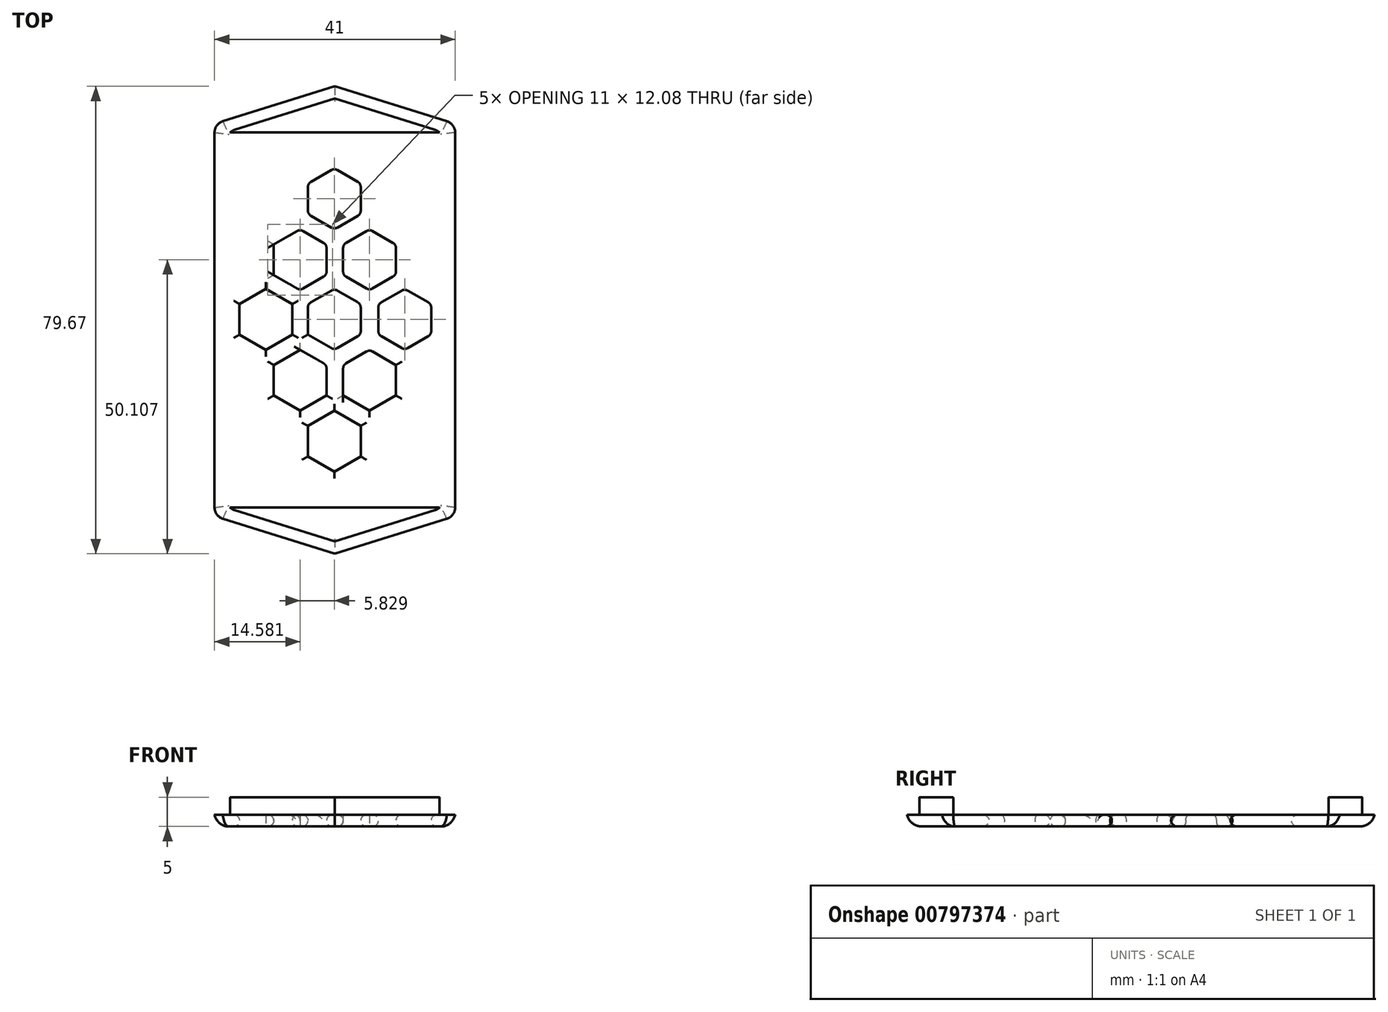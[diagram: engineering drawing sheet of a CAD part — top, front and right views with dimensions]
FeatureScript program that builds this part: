
annotation { "Feature Type Name" : "Feature", "Feature Type Description" : "" }
export const myFeature = defineFeature(function(context is Context, id is Id, definition is map)
    precondition{}
    {
        {
            var Q0;
            Q0=qCreatedBy(makeId("Top.planeOp"),FACE);
            var sketch = newSketch(context, id + "F0", { "sketchPlane" : qUnion([Q0])});
            skLineSegment(sketch, "E0", {"start": v(0.09, 44.17) * mm, "end": v(0.09, -36.2) * mm, "construction": true});
            skArc(sketch, "E1", {"start": v(-17, 32.29) * mm, "mid": v(-18.03, 31.56) * mm, "end": v(-18.41, 30.38) * mm});
            skLineSegment(sketch, "E2", {"start": v(-17, 32.29) * mm, "end": v(0.09, 37.62) * mm});
            skLineSegment(sketch, "E3", {"start": v(-66.44, -0.12) * mm, "end": v(70.75, -0.12) * mm, "construction": true});
            skLineSegment(sketch, "E4", {"start": v(-18.41, 30.38) * mm, "end": v(-18.41, -0.12) * mm});
            skLineSegment(sketch, "E5", {"start": v(-20.41, -0.12) * mm, "end": v(-20.41, 31.85) * mm});
            skLineSegment(sketch, "E6", {"start": v(0.09, 39.71) * mm, "end": v(-19, 33.76) * mm});
            skPoint(sketch, "E7.visualSharp", {"position": v(-20.41, 33.32) * mm});
            skArc(sketch, "E7.filletArc", {"start": v(-19, 33.76) * mm, "mid": v(-20.03, 33.03) * mm, "end": v(-20.41, 31.85) * mm});
            skArc(sketch, "E8.MirrorCS", {"start": v(19.18, 33.76) * mm, "mid": v(20.2, 33.03) * mm, "end": v(20.59, 31.85) * mm});
            skArc(sketch, "E9.MirrorC", {"start": v(17.18, 32.29) * mm, "mid": v(18.2, 31.56) * mm, "end": v(18.59, 30.38) * mm});
            skPoint(sketch, "E10.MirrorP", {"position": v(20.59, 33.32) * mm});
            skLineSegment(sketch, "E11.MirrorCS", {"start": v(18.59, 30.38) * mm, "end": v(18.59, -0.12) * mm});
            skLineSegment(sketch, "E12.MirrorCS", {"start": v(0.09, 39.71) * mm, "end": v(19.18, 33.76) * mm});
            skLineSegment(sketch, "E13.MirrorCS", {"start": v(17.18, 32.29) * mm, "end": v(0.09, 37.62) * mm});
            skLineSegment(sketch, "E14.MirrorCS", {"start": v(20.59, -0.12) * mm, "end": v(20.59, 31.85) * mm});
            skLineSegment(sketch, "E15.MirrorCS", {"start": v(66.62, -0.12) * mm, "end": v(-70.58, -0.12) * mm, "construction": true});
            skArc(sketch, "E16.MirrorCS", {"start": v(-19, -34) * mm, "mid": v(-20.03, -33.28) * mm, "end": v(-20.41, -32.1) * mm});
            skArc(sketch, "E17.MirrorCS", {"start": v(19.18, -34) * mm, "mid": v(20.2, -33.28) * mm, "end": v(20.59, -32.1) * mm});
            skArc(sketch, "E18.MirrorC", {"start": v(-17, -32.53) * mm, "mid": v(-18.03, -31.8) * mm, "end": v(-18.41, -30.62) * mm});
            skLineSegment(sketch, "E19.MirrorCS", {"start": v(-20.41, -0.12) * mm, "end": v(-20.41, -32.1) * mm});
            skPoint(sketch, "E20.MirrorP", {"position": v(20.59, -33.57) * mm});
            skLineSegment(sketch, "E21.MirrorCS", {"start": v(-17, -32.53) * mm, "end": v(0.09, -37.86) * mm});
            skArc(sketch, "E22.MirrorC", {"start": v(17.18, -32.53) * mm, "mid": v(18.2, -31.8) * mm, "end": v(18.59, -30.62) * mm});
            skLineSegment(sketch, "E23.MirrorCS", {"start": v(17.18, -32.53) * mm, "end": v(0.09, -37.86) * mm});
            skPoint(sketch, "E24.MirrorP", {"position": v(-20.41, -33.57) * mm});
            skLineSegment(sketch, "E25.MirrorCS", {"start": v(18.59, -30.62) * mm, "end": v(18.59, -0.12) * mm});
            skLineSegment(sketch, "E26.MirrorCS", {"start": v(20.59, -0.12) * mm, "end": v(20.59, -32.1) * mm});
            skLineSegment(sketch, "E27.MirrorCS", {"start": v(0.09, -39.96) * mm, "end": v(19.18, -34) * mm});
            skLineSegment(sketch, "E28.MirrorCS", {"start": v(-18.41, -30.62) * mm, "end": v(-18.41, -0.12) * mm});
            skLineSegment(sketch, "E29.MirrorCS", {"start": v(0.09, -39.96) * mm, "end": v(-19, -34) * mm});
            skPoint(sketch, "E30.start.orphan", {"position": v(-16.41, 28.38) * mm});
            skPoint(sketch, "E31.MirrorCS.start.orphan", {"position": v(16.59, 28.38) * mm});
            skPoint(sketch, "E32.MirrorCS.start.orphan", {"position": v(16.59, -28.62) * mm});
            skPoint(sketch, "E33.MirrorCS.start.orphan", {"position": v(-16.41, -28.62) * mm});
            skLineSegment(sketch, "E34", {"start": v(-18.41, -32.1) * mm, "end": v(18.59, -32.1) * mm});
            skLineSegment(sketch, "E35.MirrorCS", {"start": v(-18.41, 31.85) * mm, "end": v(18.59, 31.85) * mm});
            skSolve(sketch);
        }
        {
            var Q0;
            {var subQ4=sQuery(id+"F0.wireOp",EDGE,"E2");Q0=makeQuery(id+"F0.imprint","IMPRINT",FACE,{"disambiguationData":[TD([[makeQuery(id+"F0.imprint","IMPRINT",EDGE,{"derivedFrom":subQ4}),-1.0]])]});}
            var Q1;
            {var subQ4=sQuery(id+"F0.wireOp",EDGE,"E21.MirrorCS");Q1=makeQuery(id+"F0.imprint","IMPRINT",FACE,{"disambiguationData":[TD([[makeQuery(id+"F0.imprint","IMPRINT",EDGE,{"derivedFrom":subQ4}),1.0]])]});}
            extrude(context, id + "F1", {"entities" : qUnion([Q0, Q1]), "depth" : 3 * mm, "offsetDistance" : 25 * mm});
        }
        {
            var Q0;
            {var subQ12=sQuery(id+"F0.wireOp",EDGE,"E2");Q0=makeQuery(id+"F0.imprint","IMPRINT",FACE,{"disambiguationData":[TD([[makeQuery(id+"F0.imprint","IMPRINT",EDGE,{"derivedFrom":subQ12}),1.0]])]});}
            var Q1;
            {var subQ4=sQuery(id+"F0.wireOp",EDGE,"E2");Q1=makeQuery(id+"F0.imprint","IMPRINT",FACE,{"disambiguationData":[TD([[makeQuery(id+"F0.imprint","IMPRINT",EDGE,{"derivedFrom":subQ4}),-1.0]])]});}
            var Q2;
            {var subQ4=sQuery(id+"F0.wireOp",EDGE,"E21.MirrorCS");Q2=makeQuery(id+"F0.imprint","IMPRINT",FACE,{"disambiguationData":[TD([[makeQuery(id+"F0.imprint","IMPRINT",EDGE,{"derivedFrom":subQ4}),1.0]])]});}
            var Q3;
            {var subQ8=sQuery(id+"F0.wireOp",EDGE,"E4");Q3=makeQuery(id+"F0.imprint","IMPRINT",FACE,{"disambiguationData":[TD([[makeQuery(id+"F0.imprint","IMPRINT",EDGE,{"derivedFrom":subQ8}),1.0]])]});}
            extrude(context, id + "F2", {"entities" : qUnion([Q0, Q1, Q2, Q3]), "oppositeDirection" : true, "depth" : 2 * mm, "offsetDistance" : 25 * mm});
        }
        {
            var Q0;
            Q0=makeQuery(id+"F2.opExtrude","CAP_EDGE",EDGE,{"disambiguationData":[OSD([sQuery(id+"F0.wireOp",EDGE,"E14.MirrorCS"),sQuery(id+"F0.wireOp",EDGE,"E26.MirrorCS")])],"isStart":false});
            var Q1;
            Q1=makeQuery(id+"F2.opExtrude","CAP_EDGE",EDGE,{"disambiguationData":[OSD([sQuery(id+"F0.wireOp",EDGE,"E29.MirrorCS")])],"isStart":false});
            fillet(context, id + "F3", {"entities" : qUnion([Q0, Q1]), "radius" : 2.5 * mm, "tangentPropagation" : true, "allowEdgeOverflow" : false});
        }
        {
            var Q0;
            Q0=makeQuery(id+"F2.opExtrude","CAP_FACE",FACE,{"disambiguationData":[OSD([sQuery(id+"F0.wireOp",EDGE,"E5"),sQuery(id+"F0.wireOp",EDGE,"E6"),sQuery(id+"F0.wireOp",EDGE,"E7.filletArc"),sQuery(id+"F0.wireOp",EDGE,"E8.MirrorCS"),sQuery(id+"F0.wireOp",EDGE,"E12.MirrorCS"),sQuery(id+"F0.wireOp",EDGE,"E14.MirrorCS"),sQuery(id+"F0.wireOp",EDGE,"E16.MirrorCS"),sQuery(id+"F0.wireOp",EDGE,"E17.MirrorCS"),sQuery(id+"F0.wireOp",EDGE,"E19.MirrorCS"),sQuery(id+"F0.wireOp",EDGE,"E26.MirrorCS"),sQuery(id+"F0.wireOp",EDGE,"E27.MirrorCS"),sQuery(id+"F0.wireOp",EDGE,"E29.MirrorCS")])],"isStart":false});
            var sketch = newSketch(context, id + "F4", { "sketchPlane" : qUnion([Q0])});
            skCircle(sketch, "E36.cCircle", {"center": v(0, 0) * mm, "radius": 4.5 * mm, "construction": true});
            skLineSegment(sketch, "E36.0", {"start": v(-4.5, -2.6) * mm, "end": v(-4.5, 2.6) * mm});
            skLineSegment(sketch, "E36.1", {"start": v(-4.5, 2.6) * mm, "end": v(0, 5.2) * mm});
            skLineSegment(sketch, "E36.2", {"start": v(0, 5.2) * mm, "end": v(4.5, 2.6) * mm});
            skLineSegment(sketch, "E36.3", {"start": v(4.5, 2.6) * mm, "end": v(4.5, -2.6) * mm});
            skLineSegment(sketch, "E36.4", {"start": v(4.5, -2.6) * mm, "end": v(0, -5.2) * mm});
            skLineSegment(sketch, "E36.5", {"start": v(0, -5.2) * mm, "end": v(-4.5, -2.6) * mm});
            skPoint(sketch, "E36.0.midPoint", {"position": v(-4.5, 0) * mm});
            skLineSegment(sketch, "E37", {"start": v(-4.77, 9.68) * mm, "end": v(12, 0) * mm, "construction": true});
            skLineSegment(sketch, "E38.MirrorCS", {"start": v(1.5, 7.8) * mm, "end": v(6, 5.2) * mm});
            skLineSegment(sketch, "E39.MirrorCS", {"start": v(1.5, 13) * mm, "end": v(1.5, 7.8) * mm});
            skLineSegment(sketch, "E40.MirrorCS", {"start": v(6, 15.59) * mm, "end": v(1.5, 13) * mm});
            skLineSegment(sketch, "E41.MirrorCS", {"start": v(10.5, 13) * mm, "end": v(6, 15.59) * mm});
            skLineSegment(sketch, "E42.MirrorCS", {"start": v(10.5, 7.8) * mm, "end": v(10.5, 13) * mm});
            skLineSegment(sketch, "E43.MirrorCS", {"start": v(6, 5.2) * mm, "end": v(10.5, 7.8) * mm});
            skLineSegment(sketch, "E44.MirrorCS", {"start": v(-1.33, 13) * mm, "end": v(-1.33, 7.8) * mm});
            skLineSegment(sketch, "E45.MirrorCS", {"start": v(-5.83, 15.59) * mm, "end": v(-1.33, 13) * mm});
            skLineSegment(sketch, "E46.MirrorCS", {"start": v(-10.33, 13) * mm, "end": v(-5.83, 15.59) * mm});
            skLineSegment(sketch, "E47.MirrorCS", {"start": v(-10.33, 7.8) * mm, "end": v(-10.33, 13) * mm});
            skLineSegment(sketch, "E48.MirrorCS", {"start": v(-5.83, 5.2) * mm, "end": v(-10.33, 7.8) * mm});
            skLineSegment(sketch, "E49.MirrorCS", {"start": v(-1.33, 7.8) * mm, "end": v(-5.83, 5.2) * mm});
            skLineSegment(sketch, "E50.MirrorCS", {"start": v(6, -4.95) * mm, "end": v(10.5, -7.55) * mm});
            skLineSegment(sketch, "E51.MirrorCS", {"start": v(1.5, -7.55) * mm, "end": v(6, -4.95) * mm});
            skLineSegment(sketch, "E52.MirrorCS", {"start": v(1.5, -12.74) * mm, "end": v(1.5, -7.55) * mm});
            skLineSegment(sketch, "E53.MirrorCS", {"start": v(6, -15.34) * mm, "end": v(1.5, -12.74) * mm});
            skLineSegment(sketch, "E54.MirrorCS", {"start": v(10.5, -12.74) * mm, "end": v(6, -15.34) * mm});
            skLineSegment(sketch, "E55.MirrorCS", {"start": v(10.5, -7.55) * mm, "end": v(10.5, -12.74) * mm});
            skLineSegment(sketch, "E56.MirrorCS", {"start": v(-5.83, -4.95) * mm, "end": v(-10.33, -7.55) * mm});
            skLineSegment(sketch, "E57.MirrorCS", {"start": v(-1.33, -7.55) * mm, "end": v(-5.83, -4.95) * mm});
            skLineSegment(sketch, "E58.MirrorCS", {"start": v(-1.33, -12.74) * mm, "end": v(-1.33, -7.55) * mm});
            skLineSegment(sketch, "E59.MirrorCS", {"start": v(-5.83, -15.34) * mm, "end": v(-1.33, -12.74) * mm});
            skLineSegment(sketch, "E60.MirrorCS", {"start": v(-10.33, -12.74) * mm, "end": v(-5.83, -15.34) * mm});
            skLineSegment(sketch, "E61.MirrorCS", {"start": v(-10.33, -7.55) * mm, "end": v(-10.33, -12.74) * mm});
            skLineSegment(sketch, "E62", {"start": v(0, -13.61) * mm, "end": v(12.63, -20.9) * mm, "construction": true});
            skLineSegment(sketch, "E63.MirrorCS", {"start": v(4.5, -17.94) * mm, "end": v(0, -15.34) * mm});
            skLineSegment(sketch, "E64.MirrorCS", {"start": v(4.5, -23.14) * mm, "end": v(4.5, -17.94) * mm});
            skLineSegment(sketch, "E65.MirrorCS", {"start": v(0, -25.74) * mm, "end": v(4.5, -23.14) * mm});
            skLineSegment(sketch, "E66.MirrorCS", {"start": v(-4.5, -23.14) * mm, "end": v(0, -25.74) * mm});
            skLineSegment(sketch, "E67.MirrorCS", {"start": v(-4.5, -17.94) * mm, "end": v(-4.5, -23.14) * mm});
            skLineSegment(sketch, "E68.MirrorCS", {"start": v(0, -15.34) * mm, "end": v(-4.5, -17.94) * mm});
            skLineSegment(sketch, "E69.MirrorCS", {"start": v(0, 13.86) * mm, "end": v(12.63, 21.15) * mm, "construction": true});
            skLineSegment(sketch, "E70.MirrorCS", {"start": v(4.5, 18.19) * mm, "end": v(0, 15.59) * mm});
            skLineSegment(sketch, "E71.MirrorCS", {"start": v(0, 15.59) * mm, "end": v(-4.5, 18.19) * mm});
            skLineSegment(sketch, "E72.MirrorCS", {"start": v(-4.5, 18.19) * mm, "end": v(-4.5, 23.38) * mm});
            skLineSegment(sketch, "E73.MirrorCS", {"start": v(-4.5, 23.38) * mm, "end": v(0, 25.98) * mm});
            skLineSegment(sketch, "E74.MirrorCS", {"start": v(0, 25.98) * mm, "end": v(4.5, 23.38) * mm});
            skLineSegment(sketch, "E75.MirrorCS", {"start": v(4.5, 23.38) * mm, "end": v(4.5, 18.19) * mm});
            skLineSegment(sketch, "E76", {"start": v(6, 5.2) * mm, "end": v(6, -4.95) * mm, "construction": true});
            skLineSegment(sketch, "E77", {"start": v(-5.83, 5.2) * mm, "end": v(-5.83, -4.95) * mm, "construction": true});
            skLineSegment(sketch, "E78.MirrorCS", {"start": v(7.5, 2.6) * mm, "end": v(7.5, -2.6) * mm});
            skLineSegment(sketch, "E79.MirrorCS", {"start": v(7.5, -2.6) * mm, "end": v(12, -5.2) * mm});
            skLineSegment(sketch, "E80.MirrorCS", {"start": v(-6, -15.59) * mm, "end": v(2.79, -10.52) * mm, "construction": true});
            skLineSegment(sketch, "E81.MirrorCS", {"start": v(12, 5.2) * mm, "end": v(7.5, 2.6) * mm});
            skLineSegment(sketch, "E82.MirrorCS", {"start": v(16.5, 2.6) * mm, "end": v(12, 5.2) * mm});
            skLineSegment(sketch, "E83.MirrorCS", {"start": v(16.5, -2.6) * mm, "end": v(16.5, 2.6) * mm});
            skLineSegment(sketch, "E84.MirrorCS", {"start": v(12, -5.2) * mm, "end": v(16.5, -2.6) * mm});
            skLineSegment(sketch, "E85.MirrorCS", {"start": v(-7.16, -2.6) * mm, "end": v(-7.16, 2.6) * mm});
            skLineSegment(sketch, "E86.MirrorCS", {"start": v(-7.16, 2.6) * mm, "end": v(-11.66, 5.2) * mm});
            skLineSegment(sketch, "E87.MirrorCS", {"start": v(-11.66, 5.2) * mm, "end": v(-16.16, 2.6) * mm});
            skLineSegment(sketch, "E88.MirrorCS", {"start": v(-16.16, 2.6) * mm, "end": v(-16.16, -2.6) * mm});
            skLineSegment(sketch, "E89.MirrorCS", {"start": v(-16.16, -2.6) * mm, "end": v(-11.66, -5.2) * mm});
            skLineSegment(sketch, "E90.MirrorCS", {"start": v(-11.66, -5.2) * mm, "end": v(-7.16, -2.6) * mm});
            skSolve(sketch);
        }
        {
            var Q0;
            Q0=makeQuery(id+"F4.imprint","IMPRINT",FACE,{"disambiguationData":[TD([[makeQuery(id+"F4.imprint","IMPRINT",EDGE,{"derivedFrom":sQuery(id+"F4.wireOp",EDGE,"E70.MirrorCS")}),-1.0]])]});
            var Q1;
            Q1=makeQuery(id+"F4.imprint","IMPRINT",FACE,{"disambiguationData":[TD([[makeQuery(id+"F4.imprint","IMPRINT",EDGE,{"derivedFrom":sQuery(id+"F4.wireOp",EDGE,"E44.MirrorCS")}),-1.0]])]});
            var Q2;
            Q2=makeQuery(id+"F4.imprint","IMPRINT",FACE,{"disambiguationData":[TD([[makeQuery(id+"F4.imprint","IMPRINT",EDGE,{"derivedFrom":sQuery(id+"F4.wireOp",EDGE,"E85.MirrorCS")}),1.0]])]});
            var Q3;
            Q3=makeQuery(id+"F4.imprint","IMPRINT",FACE,{"disambiguationData":[TD([[makeQuery(id+"F4.imprint","IMPRINT",EDGE,{"derivedFrom":sQuery(id+"F4.wireOp",EDGE,"E56.MirrorCS")}),1.0]])]});
            var Q4;
            Q4=makeQuery(id+"F4.imprint","IMPRINT",FACE,{"disambiguationData":[TD([[makeQuery(id+"F4.imprint","IMPRINT",EDGE,{"derivedFrom":sQuery(id+"F4.wireOp",EDGE,"E63.MirrorCS")}),1.0]])]});
            var Q5;
            Q5=makeQuery(id+"F4.imprint","IMPRINT",FACE,{"disambiguationData":[TD([[makeQuery(id+"F4.imprint","IMPRINT",EDGE,{"derivedFrom":sQuery(id+"F4.wireOp",EDGE,"E50.MirrorCS")}),-1.0]])]});
            var Q6;
            Q6=makeQuery(id+"F4.imprint","IMPRINT",FACE,{"disambiguationData":[TD([[makeQuery(id+"F4.imprint","IMPRINT",EDGE,{"derivedFrom":sQuery(id+"F4.wireOp",EDGE,"E36.0")}),-1.0]])]});
            var Q7;
            Q7=makeQuery(id+"F4.imprint","IMPRINT",FACE,{"disambiguationData":[TD([[makeQuery(id+"F4.imprint","IMPRINT",EDGE,{"derivedFrom":sQuery(id+"F4.wireOp",EDGE,"E38.MirrorCS")}),1.0]])]});
            var Q8;
            Q8=makeQuery(id+"F4.imprint","IMPRINT",FACE,{"disambiguationData":[TD([[makeQuery(id+"F4.imprint","IMPRINT",EDGE,{"derivedFrom":sQuery(id+"F4.wireOp",EDGE,"E78.MirrorCS")}),1.0]])]});
            extrude(context, id + "F5", {"entities" : qUnion([Q0, Q1, Q2, Q3, Q4, Q5, Q6, Q7, Q8]), "operationType" : NewBodyOperationType.REMOVE, "oppositeDirection" : true, "depth" : 3 * mm, "offsetDistance" : 25 * mm});
        }
        {
            var Q0;
            Q0=makeQuery(id+"F5.boolean.opBoolean","COPY",EDGE,{"derivedFrom":makeQuery(id+"F5.opExtrude","CAP_EDGE",EDGE,{"disambiguationData":[OSD([sQuery(id+"F4.wireOp",EDGE,"E87.MirrorCS")])],"isStart":true})});
            var Q1;
            Q1=makeQuery(id+"F5.boolean.opBoolean","COPY",EDGE,{"derivedFrom":makeQuery(id+"F5.opExtrude","CAP_EDGE",EDGE,{"disambiguationData":[OSD([sQuery(id+"F4.wireOp",EDGE,"E88.MirrorCS")])],"isStart":true})});
            var Q2;
            Q2=makeQuery(id+"F5.boolean.opBoolean","COPY",EDGE,{"derivedFrom":makeQuery(id+"F5.opExtrude","CAP_EDGE",EDGE,{"disambiguationData":[OSD([sQuery(id+"F4.wireOp",EDGE,"E89.MirrorCS")])],"isStart":true})});
            var Q3;
            Q3=makeQuery(id+"F5.boolean.opBoolean","COPY",EDGE,{"derivedFrom":makeQuery(id+"F5.opExtrude","CAP_EDGE",EDGE,{"disambiguationData":[OSD([sQuery(id+"F4.wireOp",EDGE,"E90.MirrorCS")])],"isStart":true})});
            var Q4;
            Q4=makeQuery(id+"F5.boolean.opBoolean","COPY",EDGE,{"derivedFrom":makeQuery(id+"F5.opExtrude","CAP_EDGE",EDGE,{"disambiguationData":[OSD([sQuery(id+"F4.wireOp",EDGE,"E85.MirrorCS")])],"isStart":true})});
            var Q5;
            Q5=makeQuery(id+"F5.boolean.opBoolean","COPY",EDGE,{"derivedFrom":makeQuery(id+"F5.opExtrude","CAP_EDGE",EDGE,{"disambiguationData":[OSD([sQuery(id+"F4.wireOp",EDGE,"E86.MirrorCS")])],"isStart":true})});
            var Q6;
            Q6=makeQuery(id+"F5.boolean.opBoolean","COPY",EDGE,{"derivedFrom":makeQuery(id+"F5.opExtrude","CAP_EDGE",EDGE,{"disambiguationData":[OSD([sQuery(id+"F4.wireOp",EDGE,"E47.MirrorCS")])],"isStart":true})});
            var Q7;
            Q7=makeQuery(id+"F5.boolean.opBoolean","COPY",EDGE,{"derivedFrom":makeQuery(id+"F5.opExtrude","CAP_EDGE",EDGE,{"disambiguationData":[OSD([sQuery(id+"F4.wireOp",EDGE,"E48.MirrorCS")])],"isStart":true})});
            var Q8;
            Q8=makeQuery(id+"F5.boolean.opBoolean","COPY",EDGE,{"derivedFrom":makeQuery(id+"F5.opExtrude","CAP_EDGE",EDGE,{"disambiguationData":[OSD([sQuery(id+"F4.wireOp",EDGE,"E46.MirrorCS")])],"isStart":true})});
            var Q9;
            Q9=makeQuery(id+"F5.boolean.opBoolean","COPY",EDGE,{"derivedFrom":makeQuery(id+"F5.opExtrude","CAP_EDGE",EDGE,{"disambiguationData":[OSD([sQuery(id+"F4.wireOp",EDGE,"E45.MirrorCS")])],"isStart":true})});
            var Q10;
            Q10=makeQuery(id+"F5.boolean.opBoolean","COPY",EDGE,{"derivedFrom":makeQuery(id+"F5.opExtrude","CAP_EDGE",EDGE,{"disambiguationData":[OSD([sQuery(id+"F4.wireOp",EDGE,"E44.MirrorCS")])],"isStart":true})});
            var Q11;
            Q11=makeQuery(id+"F5.boolean.opBoolean","COPY",EDGE,{"derivedFrom":makeQuery(id+"F5.opExtrude","CAP_EDGE",EDGE,{"disambiguationData":[OSD([sQuery(id+"F4.wireOp",EDGE,"E49.MirrorCS")])],"isStart":true})});
            var Q12;
            Q12=makeQuery(id+"F5.boolean.opBoolean","COPY",EDGE,{"derivedFrom":makeQuery(id+"F5.opExtrude","CAP_EDGE",EDGE,{"disambiguationData":[OSD([sQuery(id+"F4.wireOp",EDGE,"E72.MirrorCS")])],"isStart":true})});
            var Q13;
            Q13=makeQuery(id+"F5.boolean.opBoolean","COPY",EDGE,{"derivedFrom":makeQuery(id+"F5.opExtrude","CAP_EDGE",EDGE,{"disambiguationData":[OSD([sQuery(id+"F4.wireOp",EDGE,"E71.MirrorCS")])],"isStart":true})});
            var Q14;
            Q14=makeQuery(id+"F5.boolean.opBoolean","COPY",EDGE,{"derivedFrom":makeQuery(id+"F5.opExtrude","CAP_EDGE",EDGE,{"disambiguationData":[OSD([sQuery(id+"F4.wireOp",EDGE,"E73.MirrorCS")])],"isStart":true})});
            var Q15;
            Q15=makeQuery(id+"F5.boolean.opBoolean","COPY",EDGE,{"derivedFrom":makeQuery(id+"F5.opExtrude","CAP_EDGE",EDGE,{"disambiguationData":[OSD([sQuery(id+"F4.wireOp",EDGE,"E55.MirrorCS")])],"isStart":true})});
            var Q16;
            Q16=makeQuery(id+"F5.boolean.opBoolean","INTERSECT",EDGE,{"derivedFrom":[makeQuery(id+"F2.opExtrude","CAP_FACE",FACE,{"disambiguationData":[OSD([sQuery(id+"F0.wireOp",EDGE,"E5"),sQuery(id+"F0.wireOp",EDGE,"E6"),sQuery(id+"F0.wireOp",EDGE,"E7.filletArc"),sQuery(id+"F0.wireOp",EDGE,"E8.MirrorCS"),sQuery(id+"F0.wireOp",EDGE,"E12.MirrorCS"),sQuery(id+"F0.wireOp",EDGE,"E14.MirrorCS"),sQuery(id+"F0.wireOp",EDGE,"E16.MirrorCS"),sQuery(id+"F0.wireOp",EDGE,"E17.MirrorCS"),sQuery(id+"F0.wireOp",EDGE,"E19.MirrorCS"),sQuery(id+"F0.wireOp",EDGE,"E26.MirrorCS"),sQuery(id+"F0.wireOp",EDGE,"E27.MirrorCS"),sQuery(id+"F0.wireOp",EDGE,"E29.MirrorCS")])],"isStart":true}),makeQuery(id+"F5.opExtrude","SWEPT_FACE",FACE,{"disambiguationData":[OSD([sQuery(id+"F4.wireOp",EDGE,"E50.MirrorCS")])]})]});
            var Q17;
            Q17=makeQuery(id+"F5.boolean.opBoolean","INTERSECT",EDGE,{"derivedFrom":[makeQuery(id+"F2.opExtrude","CAP_FACE",FACE,{"disambiguationData":[OSD([sQuery(id+"F0.wireOp",EDGE,"E5"),sQuery(id+"F0.wireOp",EDGE,"E6"),sQuery(id+"F0.wireOp",EDGE,"E7.filletArc"),sQuery(id+"F0.wireOp",EDGE,"E8.MirrorCS"),sQuery(id+"F0.wireOp",EDGE,"E12.MirrorCS"),sQuery(id+"F0.wireOp",EDGE,"E14.MirrorCS"),sQuery(id+"F0.wireOp",EDGE,"E16.MirrorCS"),sQuery(id+"F0.wireOp",EDGE,"E17.MirrorCS"),sQuery(id+"F0.wireOp",EDGE,"E19.MirrorCS"),sQuery(id+"F0.wireOp",EDGE,"E26.MirrorCS"),sQuery(id+"F0.wireOp",EDGE,"E27.MirrorCS"),sQuery(id+"F0.wireOp",EDGE,"E29.MirrorCS")])],"isStart":true}),makeQuery(id+"F5.opExtrude","SWEPT_FACE",FACE,{"disambiguationData":[OSD([sQuery(id+"F4.wireOp",EDGE,"E51.MirrorCS")])]})]});
            var Q18;
            Q18=makeQuery(id+"F5.boolean.opBoolean","COPY",EDGE,{"derivedFrom":makeQuery(id+"F5.opExtrude","CAP_EDGE",EDGE,{"disambiguationData":[OSD([sQuery(id+"F4.wireOp",EDGE,"E58.MirrorCS")])],"isStart":true})});
            var Q19;
            Q19=makeQuery(id+"F5.boolean.opBoolean","COPY",EDGE,{"derivedFrom":makeQuery(id+"F5.opExtrude","CAP_EDGE",EDGE,{"disambiguationData":[OSD([sQuery(id+"F4.wireOp",EDGE,"E78.MirrorCS")])],"isStart":true})});
            var Q20;
            Q20=makeQuery(id+"F5.boolean.opBoolean","INTERSECT",EDGE,{"derivedFrom":[makeQuery(id+"F2.opExtrude","CAP_FACE",FACE,{"disambiguationData":[OSD([sQuery(id+"F0.wireOp",EDGE,"E5"),sQuery(id+"F0.wireOp",EDGE,"E6"),sQuery(id+"F0.wireOp",EDGE,"E7.filletArc"),sQuery(id+"F0.wireOp",EDGE,"E8.MirrorCS"),sQuery(id+"F0.wireOp",EDGE,"E12.MirrorCS"),sQuery(id+"F0.wireOp",EDGE,"E14.MirrorCS"),sQuery(id+"F0.wireOp",EDGE,"E16.MirrorCS"),sQuery(id+"F0.wireOp",EDGE,"E17.MirrorCS"),sQuery(id+"F0.wireOp",EDGE,"E19.MirrorCS"),sQuery(id+"F0.wireOp",EDGE,"E26.MirrorCS"),sQuery(id+"F0.wireOp",EDGE,"E27.MirrorCS"),sQuery(id+"F0.wireOp",EDGE,"E29.MirrorCS")])],"isStart":true}),makeQuery(id+"F5.opExtrude","SWEPT_FACE",FACE,{"disambiguationData":[OSD([sQuery(id+"F4.wireOp",EDGE,"E52.MirrorCS")])]})]});
            var Q21;
            Q21=makeQuery(id+"F5.boolean.opBoolean","COPY",EDGE,{"derivedFrom":makeQuery(id+"F5.opExtrude","CAP_EDGE",EDGE,{"disambiguationData":[OSD([sQuery(id+"F4.wireOp",EDGE,"E59.MirrorCS")])],"isStart":true})});
            var Q22;
            Q22=makeQuery(id+"F5.boolean.opBoolean","INTERSECT",EDGE,{"derivedFrom":[makeQuery(id+"F2.opExtrude","CAP_FACE",FACE,{"disambiguationData":[OSD([sQuery(id+"F0.wireOp",EDGE,"E5"),sQuery(id+"F0.wireOp",EDGE,"E6"),sQuery(id+"F0.wireOp",EDGE,"E7.filletArc"),sQuery(id+"F0.wireOp",EDGE,"E8.MirrorCS"),sQuery(id+"F0.wireOp",EDGE,"E12.MirrorCS"),sQuery(id+"F0.wireOp",EDGE,"E14.MirrorCS"),sQuery(id+"F0.wireOp",EDGE,"E16.MirrorCS"),sQuery(id+"F0.wireOp",EDGE,"E17.MirrorCS"),sQuery(id+"F0.wireOp",EDGE,"E19.MirrorCS"),sQuery(id+"F0.wireOp",EDGE,"E26.MirrorCS"),sQuery(id+"F0.wireOp",EDGE,"E27.MirrorCS"),sQuery(id+"F0.wireOp",EDGE,"E29.MirrorCS")])],"isStart":true}),makeQuery(id+"F5.opExtrude","SWEPT_FACE",FACE,{"disambiguationData":[OSD([sQuery(id+"F4.wireOp",EDGE,"E53.MirrorCS")])]})]});
            var Q23;
            Q23=makeQuery(id+"F5.boolean.opBoolean","COPY",EDGE,{"derivedFrom":makeQuery(id+"F5.opExtrude","CAP_EDGE",EDGE,{"disambiguationData":[OSD([sQuery(id+"F4.wireOp",EDGE,"E81.MirrorCS")])],"isStart":true})});
            var Q24;
            Q24=makeQuery(id+"F5.boolean.opBoolean","INTERSECT",EDGE,{"derivedFrom":[makeQuery(id+"F2.opExtrude","CAP_FACE",FACE,{"disambiguationData":[OSD([sQuery(id+"F0.wireOp",EDGE,"E5"),sQuery(id+"F0.wireOp",EDGE,"E6"),sQuery(id+"F0.wireOp",EDGE,"E7.filletArc"),sQuery(id+"F0.wireOp",EDGE,"E8.MirrorCS"),sQuery(id+"F0.wireOp",EDGE,"E12.MirrorCS"),sQuery(id+"F0.wireOp",EDGE,"E14.MirrorCS"),sQuery(id+"F0.wireOp",EDGE,"E16.MirrorCS"),sQuery(id+"F0.wireOp",EDGE,"E17.MirrorCS"),sQuery(id+"F0.wireOp",EDGE,"E19.MirrorCS"),sQuery(id+"F0.wireOp",EDGE,"E26.MirrorCS"),sQuery(id+"F0.wireOp",EDGE,"E27.MirrorCS"),sQuery(id+"F0.wireOp",EDGE,"E29.MirrorCS")])],"isStart":true}),makeQuery(id+"F5.opExtrude","SWEPT_FACE",FACE,{"disambiguationData":[OSD([sQuery(id+"F4.wireOp",EDGE,"E54.MirrorCS")])]})]});
            var Q25;
            Q25=makeQuery(id+"F5.boolean.opBoolean","INTERSECT",EDGE,{"derivedFrom":[makeQuery(id+"F2.opExtrude","CAP_FACE",FACE,{"disambiguationData":[OSD([sQuery(id+"F0.wireOp",EDGE,"E5"),sQuery(id+"F0.wireOp",EDGE,"E6"),sQuery(id+"F0.wireOp",EDGE,"E7.filletArc"),sQuery(id+"F0.wireOp",EDGE,"E8.MirrorCS"),sQuery(id+"F0.wireOp",EDGE,"E12.MirrorCS"),sQuery(id+"F0.wireOp",EDGE,"E14.MirrorCS"),sQuery(id+"F0.wireOp",EDGE,"E16.MirrorCS"),sQuery(id+"F0.wireOp",EDGE,"E17.MirrorCS"),sQuery(id+"F0.wireOp",EDGE,"E19.MirrorCS"),sQuery(id+"F0.wireOp",EDGE,"E26.MirrorCS"),sQuery(id+"F0.wireOp",EDGE,"E27.MirrorCS"),sQuery(id+"F0.wireOp",EDGE,"E29.MirrorCS")])],"isStart":true}),makeQuery(id+"F5.opExtrude","SWEPT_FACE",FACE,{"disambiguationData":[OSD([sQuery(id+"F4.wireOp",EDGE,"E55.MirrorCS")])]})]});
            var Q26;
            Q26=makeQuery(id+"F5.boolean.opBoolean","COPY",EDGE,{"derivedFrom":makeQuery(id+"F5.opExtrude","CAP_EDGE",EDGE,{"disambiguationData":[OSD([sQuery(id+"F4.wireOp",EDGE,"E83.MirrorCS")])],"isStart":true})});
            var Q27;
            Q27=makeQuery(id+"F5.boolean.opBoolean","COPY",EDGE,{"derivedFrom":makeQuery(id+"F5.opExtrude","CAP_EDGE",EDGE,{"disambiguationData":[OSD([sQuery(id+"F4.wireOp",EDGE,"E64.MirrorCS")])],"isStart":true})});
            var Q28;
            Q28=makeQuery(id+"F5.boolean.opBoolean","COPY",EDGE,{"derivedFrom":makeQuery(id+"F5.opExtrude","CAP_EDGE",EDGE,{"disambiguationData":[OSD([sQuery(id+"F4.wireOp",EDGE,"E84.MirrorCS")])],"isStart":true})});
            var Q29;
            Q29=makeQuery(id+"F5.boolean.opBoolean","INTERSECT",EDGE,{"derivedFrom":[makeQuery(id+"F2.opExtrude","CAP_FACE",FACE,{"disambiguationData":[OSD([sQuery(id+"F0.wireOp",EDGE,"E5"),sQuery(id+"F0.wireOp",EDGE,"E6"),sQuery(id+"F0.wireOp",EDGE,"E7.filletArc"),sQuery(id+"F0.wireOp",EDGE,"E8.MirrorCS"),sQuery(id+"F0.wireOp",EDGE,"E12.MirrorCS"),sQuery(id+"F0.wireOp",EDGE,"E14.MirrorCS"),sQuery(id+"F0.wireOp",EDGE,"E16.MirrorCS"),sQuery(id+"F0.wireOp",EDGE,"E17.MirrorCS"),sQuery(id+"F0.wireOp",EDGE,"E19.MirrorCS"),sQuery(id+"F0.wireOp",EDGE,"E26.MirrorCS"),sQuery(id+"F0.wireOp",EDGE,"E27.MirrorCS"),sQuery(id+"F0.wireOp",EDGE,"E29.MirrorCS")])],"isStart":true}),makeQuery(id+"F5.opExtrude","SWEPT_FACE",FACE,{"disambiguationData":[OSD([sQuery(id+"F4.wireOp",EDGE,"E78.MirrorCS")])]})]});
            var Q30;
            Q30=makeQuery(id+"F5.boolean.opBoolean","INTERSECT",EDGE,{"derivedFrom":[makeQuery(id+"F2.opExtrude","CAP_FACE",FACE,{"disambiguationData":[OSD([sQuery(id+"F0.wireOp",EDGE,"E5"),sQuery(id+"F0.wireOp",EDGE,"E6"),sQuery(id+"F0.wireOp",EDGE,"E7.filletArc"),sQuery(id+"F0.wireOp",EDGE,"E8.MirrorCS"),sQuery(id+"F0.wireOp",EDGE,"E12.MirrorCS"),sQuery(id+"F0.wireOp",EDGE,"E14.MirrorCS"),sQuery(id+"F0.wireOp",EDGE,"E16.MirrorCS"),sQuery(id+"F0.wireOp",EDGE,"E17.MirrorCS"),sQuery(id+"F0.wireOp",EDGE,"E19.MirrorCS"),sQuery(id+"F0.wireOp",EDGE,"E26.MirrorCS"),sQuery(id+"F0.wireOp",EDGE,"E27.MirrorCS"),sQuery(id+"F0.wireOp",EDGE,"E29.MirrorCS")])],"isStart":true}),makeQuery(id+"F5.opExtrude","SWEPT_FACE",FACE,{"disambiguationData":[OSD([sQuery(id+"F4.wireOp",EDGE,"E43.MirrorCS")])]})]});
            var Q31;
            Q31=makeQuery(id+"F5.boolean.opBoolean","COPY",EDGE,{"derivedFrom":makeQuery(id+"F5.opExtrude","CAP_EDGE",EDGE,{"disambiguationData":[OSD([sQuery(id+"F4.wireOp",EDGE,"E36.2")])],"isStart":true})});
            var Q32;
            Q32=makeQuery(id+"F5.boolean.opBoolean","COPY",EDGE,{"derivedFrom":makeQuery(id+"F5.opExtrude","CAP_EDGE",EDGE,{"disambiguationData":[OSD([sQuery(id+"F4.wireOp",EDGE,"E50.MirrorCS")])],"isStart":true})});
            var Q33;
            Q33=makeQuery(id+"F5.boolean.opBoolean","INTERSECT",EDGE,{"derivedFrom":[makeQuery(id+"F2.opExtrude","CAP_FACE",FACE,{"disambiguationData":[OSD([sQuery(id+"F0.wireOp",EDGE,"E5"),sQuery(id+"F0.wireOp",EDGE,"E6"),sQuery(id+"F0.wireOp",EDGE,"E7.filletArc"),sQuery(id+"F0.wireOp",EDGE,"E8.MirrorCS"),sQuery(id+"F0.wireOp",EDGE,"E12.MirrorCS"),sQuery(id+"F0.wireOp",EDGE,"E14.MirrorCS"),sQuery(id+"F0.wireOp",EDGE,"E16.MirrorCS"),sQuery(id+"F0.wireOp",EDGE,"E17.MirrorCS"),sQuery(id+"F0.wireOp",EDGE,"E19.MirrorCS"),sQuery(id+"F0.wireOp",EDGE,"E26.MirrorCS"),sQuery(id+"F0.wireOp",EDGE,"E27.MirrorCS"),sQuery(id+"F0.wireOp",EDGE,"E29.MirrorCS")])],"isStart":true}),makeQuery(id+"F5.opExtrude","SWEPT_FACE",FACE,{"disambiguationData":[OSD([sQuery(id+"F4.wireOp",EDGE,"E44.MirrorCS")])]})]});
            var Q34;
            Q34=makeQuery(id+"F5.boolean.opBoolean","COPY",EDGE,{"derivedFrom":makeQuery(id+"F5.opExtrude","CAP_EDGE",EDGE,{"disambiguationData":[OSD([sQuery(id+"F4.wireOp",EDGE,"E36.3")])],"isStart":true})});
            var Q35;
            Q35=makeQuery(id+"F5.boolean.opBoolean","COPY",EDGE,{"derivedFrom":makeQuery(id+"F5.opExtrude","CAP_EDGE",EDGE,{"disambiguationData":[OSD([sQuery(id+"F4.wireOp",EDGE,"E51.MirrorCS")])],"isStart":true})});
            var Q36;
            Q36=makeQuery(id+"F5.boolean.opBoolean","COPY",EDGE,{"derivedFrom":makeQuery(id+"F5.opExtrude","CAP_EDGE",EDGE,{"disambiguationData":[OSD([sQuery(id+"F4.wireOp",EDGE,"E68.MirrorCS")])],"isStart":true})});
            var Q37;
            Q37=makeQuery(id+"F5.boolean.opBoolean","COPY",EDGE,{"derivedFrom":makeQuery(id+"F5.opExtrude","CAP_EDGE",EDGE,{"disambiguationData":[OSD([sQuery(id+"F4.wireOp",EDGE,"E52.MirrorCS")])],"isStart":true})});
            var Q38;
            Q38=makeQuery(id+"F5.boolean.opBoolean","INTERSECT",EDGE,{"derivedFrom":[makeQuery(id+"F2.opExtrude","CAP_FACE",FACE,{"disambiguationData":[OSD([sQuery(id+"F0.wireOp",EDGE,"E5"),sQuery(id+"F0.wireOp",EDGE,"E6"),sQuery(id+"F0.wireOp",EDGE,"E7.filletArc"),sQuery(id+"F0.wireOp",EDGE,"E8.MirrorCS"),sQuery(id+"F0.wireOp",EDGE,"E12.MirrorCS"),sQuery(id+"F0.wireOp",EDGE,"E14.MirrorCS"),sQuery(id+"F0.wireOp",EDGE,"E16.MirrorCS"),sQuery(id+"F0.wireOp",EDGE,"E17.MirrorCS"),sQuery(id+"F0.wireOp",EDGE,"E19.MirrorCS"),sQuery(id+"F0.wireOp",EDGE,"E26.MirrorCS"),sQuery(id+"F0.wireOp",EDGE,"E27.MirrorCS"),sQuery(id+"F0.wireOp",EDGE,"E29.MirrorCS")])],"isStart":true}),makeQuery(id+"F5.opExtrude","SWEPT_FACE",FACE,{"disambiguationData":[OSD([sQuery(id+"F4.wireOp",EDGE,"E83.MirrorCS")])]})]});
            var Q39;
            Q39=makeQuery(id+"F5.boolean.opBoolean","COPY",EDGE,{"derivedFrom":makeQuery(id+"F5.opExtrude","CAP_EDGE",EDGE,{"disambiguationData":[OSD([sQuery(id+"F4.wireOp",EDGE,"E53.MirrorCS")])],"isStart":true})});
            var Q40;
            Q40=makeQuery(id+"F5.boolean.opBoolean","INTERSECT",EDGE,{"derivedFrom":[makeQuery(id+"F2.opExtrude","CAP_FACE",FACE,{"disambiguationData":[OSD([sQuery(id+"F0.wireOp",EDGE,"E5"),sQuery(id+"F0.wireOp",EDGE,"E6"),sQuery(id+"F0.wireOp",EDGE,"E7.filletArc"),sQuery(id+"F0.wireOp",EDGE,"E8.MirrorCS"),sQuery(id+"F0.wireOp",EDGE,"E12.MirrorCS"),sQuery(id+"F0.wireOp",EDGE,"E14.MirrorCS"),sQuery(id+"F0.wireOp",EDGE,"E16.MirrorCS"),sQuery(id+"F0.wireOp",EDGE,"E17.MirrorCS"),sQuery(id+"F0.wireOp",EDGE,"E19.MirrorCS"),sQuery(id+"F0.wireOp",EDGE,"E26.MirrorCS"),sQuery(id+"F0.wireOp",EDGE,"E27.MirrorCS"),sQuery(id+"F0.wireOp",EDGE,"E29.MirrorCS")])],"isStart":true}),makeQuery(id+"F5.opExtrude","SWEPT_FACE",FACE,{"disambiguationData":[OSD([sQuery(id+"F4.wireOp",EDGE,"E84.MirrorCS")])]})]});
            var Q41;
            Q41=makeQuery(id+"F5.boolean.opBoolean","COPY",EDGE,{"derivedFrom":makeQuery(id+"F5.opExtrude","CAP_EDGE",EDGE,{"disambiguationData":[OSD([sQuery(id+"F4.wireOp",EDGE,"E54.MirrorCS")])],"isStart":true})});
            var Q42;
            Q42=makeQuery(id+"F5.boolean.opBoolean","INTERSECT",EDGE,{"derivedFrom":[makeQuery(id+"F2.opExtrude","CAP_FACE",FACE,{"disambiguationData":[OSD([sQuery(id+"F0.wireOp",EDGE,"E5"),sQuery(id+"F0.wireOp",EDGE,"E6"),sQuery(id+"F0.wireOp",EDGE,"E7.filletArc"),sQuery(id+"F0.wireOp",EDGE,"E8.MirrorCS"),sQuery(id+"F0.wireOp",EDGE,"E12.MirrorCS"),sQuery(id+"F0.wireOp",EDGE,"E14.MirrorCS"),sQuery(id+"F0.wireOp",EDGE,"E16.MirrorCS"),sQuery(id+"F0.wireOp",EDGE,"E17.MirrorCS"),sQuery(id+"F0.wireOp",EDGE,"E19.MirrorCS"),sQuery(id+"F0.wireOp",EDGE,"E26.MirrorCS"),sQuery(id+"F0.wireOp",EDGE,"E27.MirrorCS"),sQuery(id+"F0.wireOp",EDGE,"E29.MirrorCS")])],"isStart":true}),makeQuery(id+"F5.opExtrude","SWEPT_FACE",FACE,{"disambiguationData":[OSD([sQuery(id+"F4.wireOp",EDGE,"E36.0")])]})]});
            var Q43;
            Q43=makeQuery(id+"F5.boolean.opBoolean","COPY",EDGE,{"derivedFrom":makeQuery(id+"F5.opExtrude","SWEPT_EDGE",EDGE,{"disambiguationData":[OSD([sQuery(id+"F4.wireOp",EDGE,"E44.MirrorCS"),sQuery(id+"F4.wireOp",EDGE,"E49.MirrorCS")])]})});
            var Q44;
            Q44=makeQuery(id+"F5.boolean.opBoolean","COPY",EDGE,{"derivedFrom":makeQuery(id+"F5.opExtrude","SWEPT_EDGE",EDGE,{"disambiguationData":[OSD([sQuery(id+"F4.wireOp",EDGE,"E36.0"),sQuery(id+"F4.wireOp",EDGE,"E36.5")])]})});
            var Q45;
            Q45=makeQuery(id+"F5.boolean.opBoolean","COPY",EDGE,{"derivedFrom":makeQuery(id+"F5.opExtrude","SWEPT_EDGE",EDGE,{"disambiguationData":[OSD([sQuery(id+"F4.wireOp",EDGE,"E36.1"),sQuery(id+"F4.wireOp",EDGE,"E36.2")])]})});
            var Q46;
            Q46=makeQuery(id+"F5.boolean.opBoolean","COPY",EDGE,{"derivedFrom":makeQuery(id+"F5.opExtrude","SWEPT_EDGE",EDGE,{"disambiguationData":[OSD([sQuery(id+"F4.wireOp",EDGE,"E36.2"),sQuery(id+"F4.wireOp",EDGE,"E36.3")])]})});
            var Q47;
            Q47=makeQuery(id+"F5.boolean.opBoolean","COPY",EDGE,{"derivedFrom":makeQuery(id+"F5.opExtrude","SWEPT_EDGE",EDGE,{"disambiguationData":[OSD([sQuery(id+"F4.wireOp",EDGE,"E38.MirrorCS"),sQuery(id+"F4.wireOp",EDGE,"E39.MirrorCS")])]})});
            var Q48;
            Q48=makeQuery(id+"F5.boolean.opBoolean","COPY",EDGE,{"derivedFrom":makeQuery(id+"F5.opExtrude","SWEPT_EDGE",EDGE,{"disambiguationData":[OSD([sQuery(id+"F4.wireOp",EDGE,"E38.MirrorCS"),sQuery(id+"F4.wireOp",EDGE,"E43.MirrorCS")])]})});
            var Q49;
            Q49=makeQuery(id+"F5.boolean.opBoolean","COPY",EDGE,{"derivedFrom":makeQuery(id+"F5.opExtrude","SWEPT_EDGE",EDGE,{"disambiguationData":[OSD([sQuery(id+"F4.wireOp",EDGE,"E81.MirrorCS"),sQuery(id+"F4.wireOp",EDGE,"E82.MirrorCS")])]})});
            var Q50;
            Q50=makeQuery(id+"F5.boolean.opBoolean","INTERSECT",EDGE,{"derivedFrom":[makeQuery(id+"F2.opExtrude","CAP_FACE",FACE,{"disambiguationData":[OSD([sQuery(id+"F0.wireOp",EDGE,"E5"),sQuery(id+"F0.wireOp",EDGE,"E6"),sQuery(id+"F0.wireOp",EDGE,"E7.filletArc"),sQuery(id+"F0.wireOp",EDGE,"E8.MirrorCS"),sQuery(id+"F0.wireOp",EDGE,"E12.MirrorCS"),sQuery(id+"F0.wireOp",EDGE,"E14.MirrorCS"),sQuery(id+"F0.wireOp",EDGE,"E16.MirrorCS"),sQuery(id+"F0.wireOp",EDGE,"E17.MirrorCS"),sQuery(id+"F0.wireOp",EDGE,"E19.MirrorCS"),sQuery(id+"F0.wireOp",EDGE,"E26.MirrorCS"),sQuery(id+"F0.wireOp",EDGE,"E27.MirrorCS"),sQuery(id+"F0.wireOp",EDGE,"E29.MirrorCS")])],"isStart":true}),makeQuery(id+"F5.opExtrude","SWEPT_FACE",FACE,{"disambiguationData":[OSD([sQuery(id+"F4.wireOp",EDGE,"E36.1")])]})]});
            var Q51;
            Q51=makeQuery(id+"F5.boolean.opBoolean","INTERSECT",EDGE,{"derivedFrom":[makeQuery(id+"F2.opExtrude","CAP_FACE",FACE,{"disambiguationData":[OSD([sQuery(id+"F0.wireOp",EDGE,"E5"),sQuery(id+"F0.wireOp",EDGE,"E6"),sQuery(id+"F0.wireOp",EDGE,"E7.filletArc"),sQuery(id+"F0.wireOp",EDGE,"E8.MirrorCS"),sQuery(id+"F0.wireOp",EDGE,"E12.MirrorCS"),sQuery(id+"F0.wireOp",EDGE,"E14.MirrorCS"),sQuery(id+"F0.wireOp",EDGE,"E16.MirrorCS"),sQuery(id+"F0.wireOp",EDGE,"E17.MirrorCS"),sQuery(id+"F0.wireOp",EDGE,"E19.MirrorCS"),sQuery(id+"F0.wireOp",EDGE,"E26.MirrorCS"),sQuery(id+"F0.wireOp",EDGE,"E27.MirrorCS"),sQuery(id+"F0.wireOp",EDGE,"E29.MirrorCS")])],"isStart":true}),makeQuery(id+"F5.opExtrude","SWEPT_FACE",FACE,{"disambiguationData":[OSD([sQuery(id+"F4.wireOp",EDGE,"E66.MirrorCS")])]})]});
            var Q52;
            Q52=makeQuery(id+"F5.boolean.opBoolean","COPY",EDGE,{"derivedFrom":makeQuery(id+"F5.opExtrude","SWEPT_EDGE",EDGE,{"disambiguationData":[OSD([sQuery(id+"F4.wireOp",EDGE,"E63.MirrorCS"),sQuery(id+"F4.wireOp",EDGE,"E64.MirrorCS")])]})});
            var Q53;
            Q53=makeQuery(id+"F5.boolean.opBoolean","COPY",EDGE,{"derivedFrom":makeQuery(id+"F5.opExtrude","SWEPT_EDGE",EDGE,{"disambiguationData":[OSD([sQuery(id+"F4.wireOp",EDGE,"E82.MirrorCS"),sQuery(id+"F4.wireOp",EDGE,"E83.MirrorCS")])]})});
            var Q54;
            Q54=makeQuery(id+"F5.boolean.opBoolean","INTERSECT",EDGE,{"derivedFrom":[makeQuery(id+"F2.opExtrude","CAP_FACE",FACE,{"disambiguationData":[OSD([sQuery(id+"F0.wireOp",EDGE,"E5"),sQuery(id+"F0.wireOp",EDGE,"E6"),sQuery(id+"F0.wireOp",EDGE,"E7.filletArc"),sQuery(id+"F0.wireOp",EDGE,"E8.MirrorCS"),sQuery(id+"F0.wireOp",EDGE,"E12.MirrorCS"),sQuery(id+"F0.wireOp",EDGE,"E14.MirrorCS"),sQuery(id+"F0.wireOp",EDGE,"E16.MirrorCS"),sQuery(id+"F0.wireOp",EDGE,"E17.MirrorCS"),sQuery(id+"F0.wireOp",EDGE,"E19.MirrorCS"),sQuery(id+"F0.wireOp",EDGE,"E26.MirrorCS"),sQuery(id+"F0.wireOp",EDGE,"E27.MirrorCS"),sQuery(id+"F0.wireOp",EDGE,"E29.MirrorCS")])],"isStart":true}),makeQuery(id+"F5.opExtrude","SWEPT_FACE",FACE,{"disambiguationData":[OSD([sQuery(id+"F4.wireOp",EDGE,"E36.2")])]})]});
            var Q55;
            Q55=makeQuery(id+"F5.boolean.opBoolean","INTERSECT",EDGE,{"derivedFrom":[makeQuery(id+"F2.opExtrude","CAP_FACE",FACE,{"disambiguationData":[OSD([sQuery(id+"F0.wireOp",EDGE,"E5"),sQuery(id+"F0.wireOp",EDGE,"E6"),sQuery(id+"F0.wireOp",EDGE,"E7.filletArc"),sQuery(id+"F0.wireOp",EDGE,"E8.MirrorCS"),sQuery(id+"F0.wireOp",EDGE,"E12.MirrorCS"),sQuery(id+"F0.wireOp",EDGE,"E14.MirrorCS"),sQuery(id+"F0.wireOp",EDGE,"E16.MirrorCS"),sQuery(id+"F0.wireOp",EDGE,"E17.MirrorCS"),sQuery(id+"F0.wireOp",EDGE,"E19.MirrorCS"),sQuery(id+"F0.wireOp",EDGE,"E26.MirrorCS"),sQuery(id+"F0.wireOp",EDGE,"E27.MirrorCS"),sQuery(id+"F0.wireOp",EDGE,"E29.MirrorCS")])],"isStart":true}),makeQuery(id+"F5.opExtrude","SWEPT_FACE",FACE,{"disambiguationData":[OSD([sQuery(id+"F4.wireOp",EDGE,"E67.MirrorCS")])]})]});
            var Q56;
            Q56=makeQuery(id+"F5.boolean.opBoolean","COPY",EDGE,{"derivedFrom":makeQuery(id+"F5.opExtrude","SWEPT_EDGE",EDGE,{"disambiguationData":[OSD([sQuery(id+"F4.wireOp",EDGE,"E63.MirrorCS"),sQuery(id+"F4.wireOp",EDGE,"E68.MirrorCS")])]})});
            var Q57;
            Q57=makeQuery(id+"F5.boolean.opBoolean","COPY",EDGE,{"derivedFrom":makeQuery(id+"F5.opExtrude","SWEPT_EDGE",EDGE,{"disambiguationData":[OSD([sQuery(id+"F4.wireOp",EDGE,"E83.MirrorCS"),sQuery(id+"F4.wireOp",EDGE,"E84.MirrorCS")])]})});
            var Q58;
            Q58=makeQuery(id+"F5.boolean.opBoolean","COPY",EDGE,{"derivedFrom":makeQuery(id+"F5.opExtrude","CAP_EDGE",EDGE,{"disambiguationData":[OSD([sQuery(id+"F4.wireOp",EDGE,"E57.MirrorCS")])],"isStart":true})});
            var Q59;
            Q59=makeQuery(id+"F5.boolean.opBoolean","INTERSECT",EDGE,{"derivedFrom":[makeQuery(id+"F2.opExtrude","CAP_FACE",FACE,{"disambiguationData":[OSD([sQuery(id+"F0.wireOp",EDGE,"E5"),sQuery(id+"F0.wireOp",EDGE,"E6"),sQuery(id+"F0.wireOp",EDGE,"E7.filletArc"),sQuery(id+"F0.wireOp",EDGE,"E8.MirrorCS"),sQuery(id+"F0.wireOp",EDGE,"E12.MirrorCS"),sQuery(id+"F0.wireOp",EDGE,"E14.MirrorCS"),sQuery(id+"F0.wireOp",EDGE,"E16.MirrorCS"),sQuery(id+"F0.wireOp",EDGE,"E17.MirrorCS"),sQuery(id+"F0.wireOp",EDGE,"E19.MirrorCS"),sQuery(id+"F0.wireOp",EDGE,"E26.MirrorCS"),sQuery(id+"F0.wireOp",EDGE,"E27.MirrorCS"),sQuery(id+"F0.wireOp",EDGE,"E29.MirrorCS")])],"isStart":true}),makeQuery(id+"F5.opExtrude","SWEPT_FACE",FACE,{"disambiguationData":[OSD([sQuery(id+"F4.wireOp",EDGE,"E36.3")])]})]});
            var Q60;
            Q60=makeQuery(id+"F5.boolean.opBoolean","INTERSECT",EDGE,{"derivedFrom":[makeQuery(id+"F2.opExtrude","CAP_FACE",FACE,{"disambiguationData":[OSD([sQuery(id+"F0.wireOp",EDGE,"E5"),sQuery(id+"F0.wireOp",EDGE,"E6"),sQuery(id+"F0.wireOp",EDGE,"E7.filletArc"),sQuery(id+"F0.wireOp",EDGE,"E8.MirrorCS"),sQuery(id+"F0.wireOp",EDGE,"E12.MirrorCS"),sQuery(id+"F0.wireOp",EDGE,"E14.MirrorCS"),sQuery(id+"F0.wireOp",EDGE,"E16.MirrorCS"),sQuery(id+"F0.wireOp",EDGE,"E17.MirrorCS"),sQuery(id+"F0.wireOp",EDGE,"E19.MirrorCS"),sQuery(id+"F0.wireOp",EDGE,"E26.MirrorCS"),sQuery(id+"F0.wireOp",EDGE,"E27.MirrorCS"),sQuery(id+"F0.wireOp",EDGE,"E29.MirrorCS")])],"isStart":true}),makeQuery(id+"F5.opExtrude","SWEPT_FACE",FACE,{"disambiguationData":[OSD([sQuery(id+"F4.wireOp",EDGE,"E68.MirrorCS")])]})]});
            var Q61;
            Q61=makeQuery(id+"F5.boolean.opBoolean","COPY",EDGE,{"derivedFrom":makeQuery(id+"F5.opExtrude","SWEPT_EDGE",EDGE,{"disambiguationData":[OSD([sQuery(id+"F4.wireOp",EDGE,"E64.MirrorCS"),sQuery(id+"F4.wireOp",EDGE,"E65.MirrorCS")])]})});
            var Q62;
            Q62=makeQuery(id+"F5.boolean.opBoolean","INTERSECT",EDGE,{"derivedFrom":[makeQuery(id+"F2.opExtrude","CAP_FACE",FACE,{"disambiguationData":[OSD([sQuery(id+"F0.wireOp",EDGE,"E5"),sQuery(id+"F0.wireOp",EDGE,"E6"),sQuery(id+"F0.wireOp",EDGE,"E7.filletArc"),sQuery(id+"F0.wireOp",EDGE,"E8.MirrorCS"),sQuery(id+"F0.wireOp",EDGE,"E12.MirrorCS"),sQuery(id+"F0.wireOp",EDGE,"E14.MirrorCS"),sQuery(id+"F0.wireOp",EDGE,"E16.MirrorCS"),sQuery(id+"F0.wireOp",EDGE,"E17.MirrorCS"),sQuery(id+"F0.wireOp",EDGE,"E19.MirrorCS"),sQuery(id+"F0.wireOp",EDGE,"E26.MirrorCS"),sQuery(id+"F0.wireOp",EDGE,"E27.MirrorCS"),sQuery(id+"F0.wireOp",EDGE,"E29.MirrorCS")])],"isStart":true}),makeQuery(id+"F5.opExtrude","SWEPT_FACE",FACE,{"disambiguationData":[OSD([sQuery(id+"F4.wireOp",EDGE,"E36.4")])]})]});
            var Q63;
            Q63=makeQuery(id+"F5.boolean.opBoolean","COPY",EDGE,{"derivedFrom":makeQuery(id+"F5.opExtrude","SWEPT_EDGE",EDGE,{"disambiguationData":[OSD([sQuery(id+"F4.wireOp",EDGE,"E65.MirrorCS"),sQuery(id+"F4.wireOp",EDGE,"E66.MirrorCS")])]})});
            var Q64;
            Q64=makeQuery(id+"F5.boolean.opBoolean","COPY",EDGE,{"derivedFrom":makeQuery(id+"F5.opExtrude","CAP_EDGE",EDGE,{"disambiguationData":[OSD([sQuery(id+"F4.wireOp",EDGE,"E79.MirrorCS")])],"isStart":true})});
            var Q65;
            Q65=makeQuery(id+"F5.boolean.opBoolean","COPY",EDGE,{"derivedFrom":makeQuery(id+"F5.opExtrude","SWEPT_EDGE",EDGE,{"disambiguationData":[OSD([sQuery(id+"F4.wireOp",EDGE,"E50.MirrorCS"),sQuery(id+"F4.wireOp",EDGE,"E51.MirrorCS")])]})});
            var Q66;
            Q66=makeQuery(id+"F5.boolean.opBoolean","COPY",EDGE,{"derivedFrom":makeQuery(id+"F5.opExtrude","SWEPT_EDGE",EDGE,{"disambiguationData":[OSD([sQuery(id+"F4.wireOp",EDGE,"E66.MirrorCS"),sQuery(id+"F4.wireOp",EDGE,"E67.MirrorCS")])]})});
            var Q67;
            Q67=makeQuery(id+"F5.boolean.opBoolean","INTERSECT",EDGE,{"derivedFrom":[makeQuery(id+"F2.opExtrude","CAP_FACE",FACE,{"disambiguationData":[OSD([sQuery(id+"F0.wireOp",EDGE,"E5"),sQuery(id+"F0.wireOp",EDGE,"E6"),sQuery(id+"F0.wireOp",EDGE,"E7.filletArc"),sQuery(id+"F0.wireOp",EDGE,"E8.MirrorCS"),sQuery(id+"F0.wireOp",EDGE,"E12.MirrorCS"),sQuery(id+"F0.wireOp",EDGE,"E14.MirrorCS"),sQuery(id+"F0.wireOp",EDGE,"E16.MirrorCS"),sQuery(id+"F0.wireOp",EDGE,"E17.MirrorCS"),sQuery(id+"F0.wireOp",EDGE,"E19.MirrorCS"),sQuery(id+"F0.wireOp",EDGE,"E26.MirrorCS"),sQuery(id+"F0.wireOp",EDGE,"E27.MirrorCS"),sQuery(id+"F0.wireOp",EDGE,"E29.MirrorCS")])],"isStart":true}),makeQuery(id+"F5.opExtrude","SWEPT_FACE",FACE,{"disambiguationData":[OSD([sQuery(id+"F4.wireOp",EDGE,"E38.MirrorCS")])]})]});
            var Q68;
            Q68=makeQuery(id+"F5.boolean.opBoolean","COPY",EDGE,{"derivedFrom":makeQuery(id+"F5.opExtrude","SWEPT_EDGE",EDGE,{"disambiguationData":[OSD([sQuery(id+"F4.wireOp",EDGE,"E50.MirrorCS"),sQuery(id+"F4.wireOp",EDGE,"E55.MirrorCS")])]})});
            var Q69;
            Q69=makeQuery(id+"F5.boolean.opBoolean","COPY",EDGE,{"derivedFrom":makeQuery(id+"F5.opExtrude","SWEPT_EDGE",EDGE,{"disambiguationData":[OSD([sQuery(id+"F4.wireOp",EDGE,"E67.MirrorCS"),sQuery(id+"F4.wireOp",EDGE,"E68.MirrorCS")])]})});
            var Q70;
            Q70=makeQuery(id+"F5.boolean.opBoolean","COPY",EDGE,{"derivedFrom":makeQuery(id+"F5.opExtrude","CAP_EDGE",EDGE,{"disambiguationData":[OSD([sQuery(id+"F4.wireOp",EDGE,"E82.MirrorCS")])],"isStart":true})});
            var Q71;
            Q71=makeQuery(id+"F5.boolean.opBoolean","COPY",EDGE,{"derivedFrom":makeQuery(id+"F5.opExtrude","SWEPT_EDGE",EDGE,{"disambiguationData":[OSD([sQuery(id+"F4.wireOp",EDGE,"E51.MirrorCS"),sQuery(id+"F4.wireOp",EDGE,"E52.MirrorCS")])]})});
            var Q72;
            Q72=makeQuery(id+"F5.boolean.opBoolean","COPY",EDGE,{"derivedFrom":makeQuery(id+"F5.opExtrude","CAP_EDGE",EDGE,{"disambiguationData":[OSD([sQuery(id+"F4.wireOp",EDGE,"E63.MirrorCS")])],"isStart":true})});
            var Q73;
            Q73=makeQuery(id+"F5.boolean.opBoolean","COPY",EDGE,{"derivedFrom":makeQuery(id+"F5.opExtrude","SWEPT_EDGE",EDGE,{"disambiguationData":[OSD([sQuery(id+"F4.wireOp",EDGE,"E52.MirrorCS"),sQuery(id+"F4.wireOp",EDGE,"E53.MirrorCS")])]})});
            var Q74;
            Q74=makeQuery(id+"F5.boolean.opBoolean","INTERSECT",EDGE,{"derivedFrom":[makeQuery(id+"F2.opExtrude","CAP_FACE",FACE,{"disambiguationData":[OSD([sQuery(id+"F0.wireOp",EDGE,"E5"),sQuery(id+"F0.wireOp",EDGE,"E6"),sQuery(id+"F0.wireOp",EDGE,"E7.filletArc"),sQuery(id+"F0.wireOp",EDGE,"E8.MirrorCS"),sQuery(id+"F0.wireOp",EDGE,"E12.MirrorCS"),sQuery(id+"F0.wireOp",EDGE,"E14.MirrorCS"),sQuery(id+"F0.wireOp",EDGE,"E16.MirrorCS"),sQuery(id+"F0.wireOp",EDGE,"E17.MirrorCS"),sQuery(id+"F0.wireOp",EDGE,"E19.MirrorCS"),sQuery(id+"F0.wireOp",EDGE,"E26.MirrorCS"),sQuery(id+"F0.wireOp",EDGE,"E27.MirrorCS"),sQuery(id+"F0.wireOp",EDGE,"E29.MirrorCS")])],"isStart":true}),makeQuery(id+"F5.opExtrude","SWEPT_FACE",FACE,{"disambiguationData":[OSD([sQuery(id+"F4.wireOp",EDGE,"E57.MirrorCS")])]})]});
            var Q75;
            Q75=makeQuery(id+"F5.boolean.opBoolean","COPY",EDGE,{"derivedFrom":makeQuery(id+"F5.opExtrude","SWEPT_EDGE",EDGE,{"disambiguationData":[OSD([sQuery(id+"F4.wireOp",EDGE,"E53.MirrorCS"),sQuery(id+"F4.wireOp",EDGE,"E54.MirrorCS")])]})});
            var Q76;
            Q76=makeQuery(id+"F5.boolean.opBoolean","COPY",EDGE,{"derivedFrom":makeQuery(id+"F5.opExtrude","CAP_EDGE",EDGE,{"disambiguationData":[OSD([sQuery(id+"F4.wireOp",EDGE,"E65.MirrorCS")])],"isStart":true})});
            var Q77;
            Q77=makeQuery(id+"F5.boolean.opBoolean","INTERSECT",EDGE,{"derivedFrom":[makeQuery(id+"F2.opExtrude","CAP_FACE",FACE,{"disambiguationData":[OSD([sQuery(id+"F0.wireOp",EDGE,"E5"),sQuery(id+"F0.wireOp",EDGE,"E6"),sQuery(id+"F0.wireOp",EDGE,"E7.filletArc"),sQuery(id+"F0.wireOp",EDGE,"E8.MirrorCS"),sQuery(id+"F0.wireOp",EDGE,"E12.MirrorCS"),sQuery(id+"F0.wireOp",EDGE,"E14.MirrorCS"),sQuery(id+"F0.wireOp",EDGE,"E16.MirrorCS"),sQuery(id+"F0.wireOp",EDGE,"E17.MirrorCS"),sQuery(id+"F0.wireOp",EDGE,"E19.MirrorCS"),sQuery(id+"F0.wireOp",EDGE,"E26.MirrorCS"),sQuery(id+"F0.wireOp",EDGE,"E27.MirrorCS"),sQuery(id+"F0.wireOp",EDGE,"E29.MirrorCS")])],"isStart":true}),makeQuery(id+"F5.opExtrude","SWEPT_FACE",FACE,{"disambiguationData":[OSD([sQuery(id+"F4.wireOp",EDGE,"E58.MirrorCS")])]})]});
            var Q78;
            Q78=makeQuery(id+"F5.boolean.opBoolean","COPY",EDGE,{"derivedFrom":makeQuery(id+"F5.opExtrude","SWEPT_EDGE",EDGE,{"disambiguationData":[OSD([sQuery(id+"F4.wireOp",EDGE,"E54.MirrorCS"),sQuery(id+"F4.wireOp",EDGE,"E55.MirrorCS")])]})});
            var Q79;
            Q79=makeQuery(id+"F5.boolean.opBoolean","COPY",EDGE,{"derivedFrom":makeQuery(id+"F5.opExtrude","CAP_EDGE",EDGE,{"disambiguationData":[OSD([sQuery(id+"F4.wireOp",EDGE,"E66.MirrorCS")])],"isStart":true})});
            var Q80;
            Q80=makeQuery(id+"F5.boolean.opBoolean","INTERSECT",EDGE,{"derivedFrom":[makeQuery(id+"F2.opExtrude","CAP_FACE",FACE,{"disambiguationData":[OSD([sQuery(id+"F0.wireOp",EDGE,"E5"),sQuery(id+"F0.wireOp",EDGE,"E6"),sQuery(id+"F0.wireOp",EDGE,"E7.filletArc"),sQuery(id+"F0.wireOp",EDGE,"E8.MirrorCS"),sQuery(id+"F0.wireOp",EDGE,"E12.MirrorCS"),sQuery(id+"F0.wireOp",EDGE,"E14.MirrorCS"),sQuery(id+"F0.wireOp",EDGE,"E16.MirrorCS"),sQuery(id+"F0.wireOp",EDGE,"E17.MirrorCS"),sQuery(id+"F0.wireOp",EDGE,"E19.MirrorCS"),sQuery(id+"F0.wireOp",EDGE,"E26.MirrorCS"),sQuery(id+"F0.wireOp",EDGE,"E27.MirrorCS"),sQuery(id+"F0.wireOp",EDGE,"E29.MirrorCS")])],"isStart":true}),makeQuery(id+"F5.opExtrude","SWEPT_FACE",FACE,{"disambiguationData":[OSD([sQuery(id+"F4.wireOp",EDGE,"E59.MirrorCS")])]})]});
            var Q81;
            Q81=makeQuery(id+"F5.boolean.opBoolean","INTERSECT",EDGE,{"derivedFrom":[makeQuery(id+"F2.opExtrude","CAP_FACE",FACE,{"disambiguationData":[OSD([sQuery(id+"F0.wireOp",EDGE,"E5"),sQuery(id+"F0.wireOp",EDGE,"E6"),sQuery(id+"F0.wireOp",EDGE,"E7.filletArc"),sQuery(id+"F0.wireOp",EDGE,"E8.MirrorCS"),sQuery(id+"F0.wireOp",EDGE,"E12.MirrorCS"),sQuery(id+"F0.wireOp",EDGE,"E14.MirrorCS"),sQuery(id+"F0.wireOp",EDGE,"E16.MirrorCS"),sQuery(id+"F0.wireOp",EDGE,"E17.MirrorCS"),sQuery(id+"F0.wireOp",EDGE,"E19.MirrorCS"),sQuery(id+"F0.wireOp",EDGE,"E26.MirrorCS"),sQuery(id+"F0.wireOp",EDGE,"E27.MirrorCS"),sQuery(id+"F0.wireOp",EDGE,"E29.MirrorCS")])],"isStart":true}),makeQuery(id+"F5.opExtrude","SWEPT_FACE",FACE,{"disambiguationData":[OSD([sQuery(id+"F4.wireOp",EDGE,"E79.MirrorCS")])]})]});
            var Q82;
            Q82=makeQuery(id+"F5.boolean.opBoolean","COPY",EDGE,{"derivedFrom":makeQuery(id+"F5.opExtrude","CAP_EDGE",EDGE,{"disambiguationData":[OSD([sQuery(id+"F4.wireOp",EDGE,"E67.MirrorCS")])],"isStart":true})});
            var Q83;
            Q83=makeQuery(id+"F5.boolean.opBoolean","INTERSECT",EDGE,{"derivedFrom":[makeQuery(id+"F2.opExtrude","CAP_FACE",FACE,{"disambiguationData":[OSD([sQuery(id+"F0.wireOp",EDGE,"E5"),sQuery(id+"F0.wireOp",EDGE,"E6"),sQuery(id+"F0.wireOp",EDGE,"E7.filletArc"),sQuery(id+"F0.wireOp",EDGE,"E8.MirrorCS"),sQuery(id+"F0.wireOp",EDGE,"E12.MirrorCS"),sQuery(id+"F0.wireOp",EDGE,"E14.MirrorCS"),sQuery(id+"F0.wireOp",EDGE,"E16.MirrorCS"),sQuery(id+"F0.wireOp",EDGE,"E17.MirrorCS"),sQuery(id+"F0.wireOp",EDGE,"E19.MirrorCS"),sQuery(id+"F0.wireOp",EDGE,"E26.MirrorCS"),sQuery(id+"F0.wireOp",EDGE,"E27.MirrorCS"),sQuery(id+"F0.wireOp",EDGE,"E29.MirrorCS")])],"isStart":true}),makeQuery(id+"F5.opExtrude","SWEPT_FACE",FACE,{"disambiguationData":[OSD([sQuery(id+"F4.wireOp",EDGE,"E81.MirrorCS")])]})]});
            var Q84;
            Q84=makeQuery(id+"F5.boolean.opBoolean","INTERSECT",EDGE,{"derivedFrom":[makeQuery(id+"F2.opExtrude","CAP_FACE",FACE,{"disambiguationData":[OSD([sQuery(id+"F0.wireOp",EDGE,"E5"),sQuery(id+"F0.wireOp",EDGE,"E6"),sQuery(id+"F0.wireOp",EDGE,"E7.filletArc"),sQuery(id+"F0.wireOp",EDGE,"E8.MirrorCS"),sQuery(id+"F0.wireOp",EDGE,"E12.MirrorCS"),sQuery(id+"F0.wireOp",EDGE,"E14.MirrorCS"),sQuery(id+"F0.wireOp",EDGE,"E16.MirrorCS"),sQuery(id+"F0.wireOp",EDGE,"E17.MirrorCS"),sQuery(id+"F0.wireOp",EDGE,"E19.MirrorCS"),sQuery(id+"F0.wireOp",EDGE,"E26.MirrorCS"),sQuery(id+"F0.wireOp",EDGE,"E27.MirrorCS"),sQuery(id+"F0.wireOp",EDGE,"E29.MirrorCS")])],"isStart":true}),makeQuery(id+"F5.opExtrude","SWEPT_FACE",FACE,{"disambiguationData":[OSD([sQuery(id+"F4.wireOp",EDGE,"E82.MirrorCS")])]})]});
            var Q85;
            Q85=makeQuery(id+"F5.boolean.opBoolean","COPY",EDGE,{"derivedFrom":makeQuery(id+"F5.opExtrude","SWEPT_EDGE",EDGE,{"disambiguationData":[OSD([sQuery(id+"F4.wireOp",EDGE,"E78.MirrorCS"),sQuery(id+"F4.wireOp",EDGE,"E81.MirrorCS")])]})});
            var Q86;
            Q86=makeQuery(id+"F5.boolean.opBoolean","COPY",EDGE,{"derivedFrom":makeQuery(id+"F5.opExtrude","CAP_EDGE",EDGE,{"disambiguationData":[OSD([sQuery(id+"F4.wireOp",EDGE,"E36.4")])],"isStart":true})});
            var Q87;
            Q87=makeQuery(id+"F5.boolean.opBoolean","INTERSECT",EDGE,{"derivedFrom":[makeQuery(id+"F2.opExtrude","CAP_FACE",FACE,{"disambiguationData":[OSD([sQuery(id+"F0.wireOp",EDGE,"E5"),sQuery(id+"F0.wireOp",EDGE,"E6"),sQuery(id+"F0.wireOp",EDGE,"E7.filletArc"),sQuery(id+"F0.wireOp",EDGE,"E8.MirrorCS"),sQuery(id+"F0.wireOp",EDGE,"E12.MirrorCS"),sQuery(id+"F0.wireOp",EDGE,"E14.MirrorCS"),sQuery(id+"F0.wireOp",EDGE,"E16.MirrorCS"),sQuery(id+"F0.wireOp",EDGE,"E17.MirrorCS"),sQuery(id+"F0.wireOp",EDGE,"E19.MirrorCS"),sQuery(id+"F0.wireOp",EDGE,"E26.MirrorCS"),sQuery(id+"F0.wireOp",EDGE,"E27.MirrorCS"),sQuery(id+"F0.wireOp",EDGE,"E29.MirrorCS")])],"isStart":true}),makeQuery(id+"F5.opExtrude","SWEPT_FACE",FACE,{"disambiguationData":[OSD([sQuery(id+"F4.wireOp",EDGE,"E63.MirrorCS")])]})]});
            var Q88;
            Q88=makeQuery(id+"F5.boolean.opBoolean","COPY",EDGE,{"derivedFrom":makeQuery(id+"F5.opExtrude","SWEPT_EDGE",EDGE,{"disambiguationData":[OSD([sQuery(id+"F4.wireOp",EDGE,"E58.MirrorCS"),sQuery(id+"F4.wireOp",EDGE,"E59.MirrorCS")])]})});
            var Q89;
            Q89=makeQuery(id+"F5.boolean.opBoolean","COPY",EDGE,{"derivedFrom":makeQuery(id+"F5.opExtrude","SWEPT_EDGE",EDGE,{"disambiguationData":[OSD([sQuery(id+"F4.wireOp",EDGE,"E78.MirrorCS"),sQuery(id+"F4.wireOp",EDGE,"E79.MirrorCS")])]})});
            var Q90;
            Q90=makeQuery(id+"F5.boolean.opBoolean","COPY",EDGE,{"derivedFrom":makeQuery(id+"F5.opExtrude","CAP_EDGE",EDGE,{"disambiguationData":[OSD([sQuery(id+"F4.wireOp",EDGE,"E36.5")])],"isStart":true})});
            var Q91;
            Q91=makeQuery(id+"F5.boolean.opBoolean","INTERSECT",EDGE,{"derivedFrom":[makeQuery(id+"F2.opExtrude","CAP_FACE",FACE,{"disambiguationData":[OSD([sQuery(id+"F0.wireOp",EDGE,"E5"),sQuery(id+"F0.wireOp",EDGE,"E6"),sQuery(id+"F0.wireOp",EDGE,"E7.filletArc"),sQuery(id+"F0.wireOp",EDGE,"E8.MirrorCS"),sQuery(id+"F0.wireOp",EDGE,"E12.MirrorCS"),sQuery(id+"F0.wireOp",EDGE,"E14.MirrorCS"),sQuery(id+"F0.wireOp",EDGE,"E16.MirrorCS"),sQuery(id+"F0.wireOp",EDGE,"E17.MirrorCS"),sQuery(id+"F0.wireOp",EDGE,"E19.MirrorCS"),sQuery(id+"F0.wireOp",EDGE,"E26.MirrorCS"),sQuery(id+"F0.wireOp",EDGE,"E27.MirrorCS"),sQuery(id+"F0.wireOp",EDGE,"E29.MirrorCS")])],"isStart":true}),makeQuery(id+"F5.opExtrude","SWEPT_FACE",FACE,{"disambiguationData":[OSD([sQuery(id+"F4.wireOp",EDGE,"E64.MirrorCS")])]})]});
            var Q92;
            Q92=makeQuery(id+"F5.boolean.opBoolean","COPY",EDGE,{"derivedFrom":makeQuery(id+"F5.opExtrude","SWEPT_EDGE",EDGE,{"disambiguationData":[OSD([sQuery(id+"F4.wireOp",EDGE,"E59.MirrorCS"),sQuery(id+"F4.wireOp",EDGE,"E60.MirrorCS")])]})});
            var Q93;
            Q93=makeQuery(id+"F5.boolean.opBoolean","COPY",EDGE,{"derivedFrom":makeQuery(id+"F5.opExtrude","SWEPT_EDGE",EDGE,{"disambiguationData":[OSD([sQuery(id+"F4.wireOp",EDGE,"E79.MirrorCS"),sQuery(id+"F4.wireOp",EDGE,"E84.MirrorCS")])]})});
            var Q94;
            Q94=makeQuery(id+"F5.boolean.opBoolean","COPY",EDGE,{"derivedFrom":makeQuery(id+"F5.opExtrude","CAP_EDGE",EDGE,{"disambiguationData":[OSD([sQuery(id+"F4.wireOp",EDGE,"E38.MirrorCS")])],"isStart":true})});
            var Q95;
            Q95=makeQuery(id+"F5.boolean.opBoolean","INTERSECT",EDGE,{"derivedFrom":[makeQuery(id+"F2.opExtrude","CAP_FACE",FACE,{"disambiguationData":[OSD([sQuery(id+"F0.wireOp",EDGE,"E5"),sQuery(id+"F0.wireOp",EDGE,"E6"),sQuery(id+"F0.wireOp",EDGE,"E7.filletArc"),sQuery(id+"F0.wireOp",EDGE,"E8.MirrorCS"),sQuery(id+"F0.wireOp",EDGE,"E12.MirrorCS"),sQuery(id+"F0.wireOp",EDGE,"E14.MirrorCS"),sQuery(id+"F0.wireOp",EDGE,"E16.MirrorCS"),sQuery(id+"F0.wireOp",EDGE,"E17.MirrorCS"),sQuery(id+"F0.wireOp",EDGE,"E19.MirrorCS"),sQuery(id+"F0.wireOp",EDGE,"E26.MirrorCS"),sQuery(id+"F0.wireOp",EDGE,"E27.MirrorCS"),sQuery(id+"F0.wireOp",EDGE,"E29.MirrorCS")])],"isStart":true}),makeQuery(id+"F5.opExtrude","SWEPT_FACE",FACE,{"disambiguationData":[OSD([sQuery(id+"F4.wireOp",EDGE,"E65.MirrorCS")])]})]});
            var Q96;
            Q96=makeQuery(id+"F5.boolean.opBoolean","COPY",EDGE,{"derivedFrom":makeQuery(id+"F5.opExtrude","SWEPT_EDGE",EDGE,{"disambiguationData":[OSD([sQuery(id+"F4.wireOp",EDGE,"E36.3"),sQuery(id+"F4.wireOp",EDGE,"E36.4")])]})});
            var Q97;
            Q97=makeQuery(id+"F5.boolean.opBoolean","COPY",EDGE,{"derivedFrom":makeQuery(id+"F5.opExtrude","SWEPT_EDGE",EDGE,{"disambiguationData":[OSD([sQuery(id+"F4.wireOp",EDGE,"E36.4"),sQuery(id+"F4.wireOp",EDGE,"E36.5")])]})});
            var Q98;
            Q98=makeQuery(id+"F5.boolean.opBoolean","INTERSECT",EDGE,{"derivedFrom":[makeQuery(id+"F2.opExtrude","CAP_FACE",FACE,{"disambiguationData":[OSD([sQuery(id+"F0.wireOp",EDGE,"E5"),sQuery(id+"F0.wireOp",EDGE,"E6"),sQuery(id+"F0.wireOp",EDGE,"E7.filletArc"),sQuery(id+"F0.wireOp",EDGE,"E8.MirrorCS"),sQuery(id+"F0.wireOp",EDGE,"E12.MirrorCS"),sQuery(id+"F0.wireOp",EDGE,"E14.MirrorCS"),sQuery(id+"F0.wireOp",EDGE,"E16.MirrorCS"),sQuery(id+"F0.wireOp",EDGE,"E17.MirrorCS"),sQuery(id+"F0.wireOp",EDGE,"E19.MirrorCS"),sQuery(id+"F0.wireOp",EDGE,"E26.MirrorCS"),sQuery(id+"F0.wireOp",EDGE,"E27.MirrorCS"),sQuery(id+"F0.wireOp",EDGE,"E29.MirrorCS")])],"isStart":true}),makeQuery(id+"F5.opExtrude","SWEPT_FACE",FACE,{"disambiguationData":[OSD([sQuery(id+"F4.wireOp",EDGE,"E36.5")])]})]});
            var Q99;
            Q99=makeQuery(id+"F5.boolean.opBoolean","COPY",EDGE,{"derivedFrom":makeQuery(id+"F5.opExtrude","SWEPT_EDGE",EDGE,{"disambiguationData":[OSD([sQuery(id+"F4.wireOp",EDGE,"E56.MirrorCS"),sQuery(id+"F4.wireOp",EDGE,"E57.MirrorCS")])]})});
            var Q100;
            Q100=makeQuery(id+"F5.boolean.opBoolean","COPY",EDGE,{"derivedFrom":makeQuery(id+"F5.opExtrude","SWEPT_EDGE",EDGE,{"disambiguationData":[OSD([sQuery(id+"F4.wireOp",EDGE,"E57.MirrorCS"),sQuery(id+"F4.wireOp",EDGE,"E58.MirrorCS")])]})});
            var Q101;
            Q101=makeQuery(id+"F2.opExtrude","CAP_FACE",FACE,{"disambiguationData":[OSD([sQuery(id+"F0.wireOp",EDGE,"E5"),sQuery(id+"F0.wireOp",EDGE,"E6"),sQuery(id+"F0.wireOp",EDGE,"E7.filletArc"),sQuery(id+"F0.wireOp",EDGE,"E8.MirrorCS"),sQuery(id+"F0.wireOp",EDGE,"E12.MirrorCS"),sQuery(id+"F0.wireOp",EDGE,"E14.MirrorCS"),sQuery(id+"F0.wireOp",EDGE,"E16.MirrorCS"),sQuery(id+"F0.wireOp",EDGE,"E17.MirrorCS"),sQuery(id+"F0.wireOp",EDGE,"E19.MirrorCS"),sQuery(id+"F0.wireOp",EDGE,"E26.MirrorCS"),sQuery(id+"F0.wireOp",EDGE,"E27.MirrorCS"),sQuery(id+"F0.wireOp",EDGE,"E29.MirrorCS")])],"isStart":false});
            var Q102;
            Q102=makeQuery(id+"F5.boolean.opBoolean","INTERSECT",EDGE,{"derivedFrom":[makeQuery(id+"F2.opExtrude","CAP_FACE",FACE,{"disambiguationData":[OSD([sQuery(id+"F0.wireOp",EDGE,"E5"),sQuery(id+"F0.wireOp",EDGE,"E6"),sQuery(id+"F0.wireOp",EDGE,"E7.filletArc"),sQuery(id+"F0.wireOp",EDGE,"E8.MirrorCS"),sQuery(id+"F0.wireOp",EDGE,"E12.MirrorCS"),sQuery(id+"F0.wireOp",EDGE,"E14.MirrorCS"),sQuery(id+"F0.wireOp",EDGE,"E16.MirrorCS"),sQuery(id+"F0.wireOp",EDGE,"E17.MirrorCS"),sQuery(id+"F0.wireOp",EDGE,"E19.MirrorCS"),sQuery(id+"F0.wireOp",EDGE,"E26.MirrorCS"),sQuery(id+"F0.wireOp",EDGE,"E27.MirrorCS"),sQuery(id+"F0.wireOp",EDGE,"E29.MirrorCS")])],"isStart":true}),makeQuery(id+"F5.opExtrude","SWEPT_FACE",FACE,{"disambiguationData":[OSD([sQuery(id+"F4.wireOp",EDGE,"E87.MirrorCS")])]})]});
            var Q103;
            Q103=makeQuery(id+"F5.boolean.opBoolean","INTERSECT",EDGE,{"derivedFrom":[makeQuery(id+"F2.opExtrude","CAP_FACE",FACE,{"disambiguationData":[OSD([sQuery(id+"F0.wireOp",EDGE,"E5"),sQuery(id+"F0.wireOp",EDGE,"E6"),sQuery(id+"F0.wireOp",EDGE,"E7.filletArc"),sQuery(id+"F0.wireOp",EDGE,"E8.MirrorCS"),sQuery(id+"F0.wireOp",EDGE,"E12.MirrorCS"),sQuery(id+"F0.wireOp",EDGE,"E14.MirrorCS"),sQuery(id+"F0.wireOp",EDGE,"E16.MirrorCS"),sQuery(id+"F0.wireOp",EDGE,"E17.MirrorCS"),sQuery(id+"F0.wireOp",EDGE,"E19.MirrorCS"),sQuery(id+"F0.wireOp",EDGE,"E26.MirrorCS"),sQuery(id+"F0.wireOp",EDGE,"E27.MirrorCS"),sQuery(id+"F0.wireOp",EDGE,"E29.MirrorCS")])],"isStart":true}),makeQuery(id+"F5.opExtrude","SWEPT_FACE",FACE,{"disambiguationData":[OSD([sQuery(id+"F4.wireOp",EDGE,"E86.MirrorCS")])]})]});
            var Q104;
            Q104=makeQuery(id+"F5.boolean.opBoolean","INTERSECT",EDGE,{"derivedFrom":[makeQuery(id+"F2.opExtrude","CAP_FACE",FACE,{"disambiguationData":[OSD([sQuery(id+"F0.wireOp",EDGE,"E5"),sQuery(id+"F0.wireOp",EDGE,"E6"),sQuery(id+"F0.wireOp",EDGE,"E7.filletArc"),sQuery(id+"F0.wireOp",EDGE,"E8.MirrorCS"),sQuery(id+"F0.wireOp",EDGE,"E12.MirrorCS"),sQuery(id+"F0.wireOp",EDGE,"E14.MirrorCS"),sQuery(id+"F0.wireOp",EDGE,"E16.MirrorCS"),sQuery(id+"F0.wireOp",EDGE,"E17.MirrorCS"),sQuery(id+"F0.wireOp",EDGE,"E19.MirrorCS"),sQuery(id+"F0.wireOp",EDGE,"E26.MirrorCS"),sQuery(id+"F0.wireOp",EDGE,"E27.MirrorCS"),sQuery(id+"F0.wireOp",EDGE,"E29.MirrorCS")])],"isStart":true}),makeQuery(id+"F5.opExtrude","SWEPT_FACE",FACE,{"disambiguationData":[OSD([sQuery(id+"F4.wireOp",EDGE,"E85.MirrorCS")])]})]});
            var Q105;
            Q105=makeQuery(id+"F5.boolean.opBoolean","INTERSECT",EDGE,{"derivedFrom":[makeQuery(id+"F2.opExtrude","CAP_FACE",FACE,{"disambiguationData":[OSD([sQuery(id+"F0.wireOp",EDGE,"E5"),sQuery(id+"F0.wireOp",EDGE,"E6"),sQuery(id+"F0.wireOp",EDGE,"E7.filletArc"),sQuery(id+"F0.wireOp",EDGE,"E8.MirrorCS"),sQuery(id+"F0.wireOp",EDGE,"E12.MirrorCS"),sQuery(id+"F0.wireOp",EDGE,"E14.MirrorCS"),sQuery(id+"F0.wireOp",EDGE,"E16.MirrorCS"),sQuery(id+"F0.wireOp",EDGE,"E17.MirrorCS"),sQuery(id+"F0.wireOp",EDGE,"E19.MirrorCS"),sQuery(id+"F0.wireOp",EDGE,"E26.MirrorCS"),sQuery(id+"F0.wireOp",EDGE,"E27.MirrorCS"),sQuery(id+"F0.wireOp",EDGE,"E29.MirrorCS")])],"isStart":true}),makeQuery(id+"F5.opExtrude","SWEPT_FACE",FACE,{"disambiguationData":[OSD([sQuery(id+"F4.wireOp",EDGE,"E61.MirrorCS")])]})]});
            var Q106;
            Q106=makeQuery(id+"F5.boolean.opBoolean","INTERSECT",EDGE,{"derivedFrom":[makeQuery(id+"F2.opExtrude","CAP_FACE",FACE,{"disambiguationData":[OSD([sQuery(id+"F0.wireOp",EDGE,"E5"),sQuery(id+"F0.wireOp",EDGE,"E6"),sQuery(id+"F0.wireOp",EDGE,"E7.filletArc"),sQuery(id+"F0.wireOp",EDGE,"E8.MirrorCS"),sQuery(id+"F0.wireOp",EDGE,"E12.MirrorCS"),sQuery(id+"F0.wireOp",EDGE,"E14.MirrorCS"),sQuery(id+"F0.wireOp",EDGE,"E16.MirrorCS"),sQuery(id+"F0.wireOp",EDGE,"E17.MirrorCS"),sQuery(id+"F0.wireOp",EDGE,"E19.MirrorCS"),sQuery(id+"F0.wireOp",EDGE,"E26.MirrorCS"),sQuery(id+"F0.wireOp",EDGE,"E27.MirrorCS"),sQuery(id+"F0.wireOp",EDGE,"E29.MirrorCS")])],"isStart":true}),makeQuery(id+"F5.opExtrude","SWEPT_FACE",FACE,{"disambiguationData":[OSD([sQuery(id+"F4.wireOp",EDGE,"E88.MirrorCS")])]})]});
            var Q107;
            Q107=makeQuery(id+"F5.boolean.opBoolean","INTERSECT",EDGE,{"derivedFrom":[makeQuery(id+"F2.opExtrude","CAP_FACE",FACE,{"disambiguationData":[OSD([sQuery(id+"F0.wireOp",EDGE,"E5"),sQuery(id+"F0.wireOp",EDGE,"E6"),sQuery(id+"F0.wireOp",EDGE,"E7.filletArc"),sQuery(id+"F0.wireOp",EDGE,"E8.MirrorCS"),sQuery(id+"F0.wireOp",EDGE,"E12.MirrorCS"),sQuery(id+"F0.wireOp",EDGE,"E14.MirrorCS"),sQuery(id+"F0.wireOp",EDGE,"E16.MirrorCS"),sQuery(id+"F0.wireOp",EDGE,"E17.MirrorCS"),sQuery(id+"F0.wireOp",EDGE,"E19.MirrorCS"),sQuery(id+"F0.wireOp",EDGE,"E26.MirrorCS"),sQuery(id+"F0.wireOp",EDGE,"E27.MirrorCS"),sQuery(id+"F0.wireOp",EDGE,"E29.MirrorCS")])],"isStart":true}),makeQuery(id+"F5.opExtrude","SWEPT_FACE",FACE,{"disambiguationData":[OSD([sQuery(id+"F4.wireOp",EDGE,"E90.MirrorCS")])]})]});
            var Q108;
            Q108=makeQuery(id+"F5.boolean.opBoolean","INTERSECT",EDGE,{"derivedFrom":[makeQuery(id+"F2.opExtrude","CAP_FACE",FACE,{"disambiguationData":[OSD([sQuery(id+"F0.wireOp",EDGE,"E5"),sQuery(id+"F0.wireOp",EDGE,"E6"),sQuery(id+"F0.wireOp",EDGE,"E7.filletArc"),sQuery(id+"F0.wireOp",EDGE,"E8.MirrorCS"),sQuery(id+"F0.wireOp",EDGE,"E12.MirrorCS"),sQuery(id+"F0.wireOp",EDGE,"E14.MirrorCS"),sQuery(id+"F0.wireOp",EDGE,"E16.MirrorCS"),sQuery(id+"F0.wireOp",EDGE,"E17.MirrorCS"),sQuery(id+"F0.wireOp",EDGE,"E19.MirrorCS"),sQuery(id+"F0.wireOp",EDGE,"E26.MirrorCS"),sQuery(id+"F0.wireOp",EDGE,"E27.MirrorCS"),sQuery(id+"F0.wireOp",EDGE,"E29.MirrorCS")])],"isStart":true}),makeQuery(id+"F5.opExtrude","SWEPT_FACE",FACE,{"disambiguationData":[OSD([sQuery(id+"F4.wireOp",EDGE,"E89.MirrorCS")])]})]});
            var Q109;
            Q109=makeQuery(id+"F5.boolean.opBoolean","INTERSECT",EDGE,{"derivedFrom":[makeQuery(id+"F2.opExtrude","CAP_FACE",FACE,{"disambiguationData":[OSD([sQuery(id+"F0.wireOp",EDGE,"E5"),sQuery(id+"F0.wireOp",EDGE,"E6"),sQuery(id+"F0.wireOp",EDGE,"E7.filletArc"),sQuery(id+"F0.wireOp",EDGE,"E8.MirrorCS"),sQuery(id+"F0.wireOp",EDGE,"E12.MirrorCS"),sQuery(id+"F0.wireOp",EDGE,"E14.MirrorCS"),sQuery(id+"F0.wireOp",EDGE,"E16.MirrorCS"),sQuery(id+"F0.wireOp",EDGE,"E17.MirrorCS"),sQuery(id+"F0.wireOp",EDGE,"E19.MirrorCS"),sQuery(id+"F0.wireOp",EDGE,"E26.MirrorCS"),sQuery(id+"F0.wireOp",EDGE,"E27.MirrorCS"),sQuery(id+"F0.wireOp",EDGE,"E29.MirrorCS")])],"isStart":true}),makeQuery(id+"F5.opExtrude","SWEPT_FACE",FACE,{"disambiguationData":[OSD([sQuery(id+"F4.wireOp",EDGE,"E48.MirrorCS")])]})]});
            var Q110;
            Q110=makeQuery(id+"F5.boolean.opBoolean","INTERSECT",EDGE,{"derivedFrom":[makeQuery(id+"F2.opExtrude","CAP_FACE",FACE,{"disambiguationData":[OSD([sQuery(id+"F0.wireOp",EDGE,"E5"),sQuery(id+"F0.wireOp",EDGE,"E6"),sQuery(id+"F0.wireOp",EDGE,"E7.filletArc"),sQuery(id+"F0.wireOp",EDGE,"E8.MirrorCS"),sQuery(id+"F0.wireOp",EDGE,"E12.MirrorCS"),sQuery(id+"F0.wireOp",EDGE,"E14.MirrorCS"),sQuery(id+"F0.wireOp",EDGE,"E16.MirrorCS"),sQuery(id+"F0.wireOp",EDGE,"E17.MirrorCS"),sQuery(id+"F0.wireOp",EDGE,"E19.MirrorCS"),sQuery(id+"F0.wireOp",EDGE,"E26.MirrorCS"),sQuery(id+"F0.wireOp",EDGE,"E27.MirrorCS"),sQuery(id+"F0.wireOp",EDGE,"E29.MirrorCS")])],"isStart":true}),makeQuery(id+"F5.opExtrude","SWEPT_FACE",FACE,{"disambiguationData":[OSD([sQuery(id+"F4.wireOp",EDGE,"E47.MirrorCS")])]})]});
            var Q111;
            Q111=makeQuery(id+"F5.boolean.opBoolean","INTERSECT",EDGE,{"derivedFrom":[makeQuery(id+"F2.opExtrude","CAP_FACE",FACE,{"disambiguationData":[OSD([sQuery(id+"F0.wireOp",EDGE,"E5"),sQuery(id+"F0.wireOp",EDGE,"E6"),sQuery(id+"F0.wireOp",EDGE,"E7.filletArc"),sQuery(id+"F0.wireOp",EDGE,"E8.MirrorCS"),sQuery(id+"F0.wireOp",EDGE,"E12.MirrorCS"),sQuery(id+"F0.wireOp",EDGE,"E14.MirrorCS"),sQuery(id+"F0.wireOp",EDGE,"E16.MirrorCS"),sQuery(id+"F0.wireOp",EDGE,"E17.MirrorCS"),sQuery(id+"F0.wireOp",EDGE,"E19.MirrorCS"),sQuery(id+"F0.wireOp",EDGE,"E26.MirrorCS"),sQuery(id+"F0.wireOp",EDGE,"E27.MirrorCS"),sQuery(id+"F0.wireOp",EDGE,"E29.MirrorCS")])],"isStart":true}),makeQuery(id+"F5.opExtrude","SWEPT_FACE",FACE,{"disambiguationData":[OSD([sQuery(id+"F4.wireOp",EDGE,"E46.MirrorCS")])]})]});
            var Q112;
            Q112=makeQuery(id+"F5.boolean.opBoolean","INTERSECT",EDGE,{"derivedFrom":[makeQuery(id+"F2.opExtrude","CAP_FACE",FACE,{"disambiguationData":[OSD([sQuery(id+"F0.wireOp",EDGE,"E5"),sQuery(id+"F0.wireOp",EDGE,"E6"),sQuery(id+"F0.wireOp",EDGE,"E7.filletArc"),sQuery(id+"F0.wireOp",EDGE,"E8.MirrorCS"),sQuery(id+"F0.wireOp",EDGE,"E12.MirrorCS"),sQuery(id+"F0.wireOp",EDGE,"E14.MirrorCS"),sQuery(id+"F0.wireOp",EDGE,"E16.MirrorCS"),sQuery(id+"F0.wireOp",EDGE,"E17.MirrorCS"),sQuery(id+"F0.wireOp",EDGE,"E19.MirrorCS"),sQuery(id+"F0.wireOp",EDGE,"E26.MirrorCS"),sQuery(id+"F0.wireOp",EDGE,"E27.MirrorCS"),sQuery(id+"F0.wireOp",EDGE,"E29.MirrorCS")])],"isStart":true}),makeQuery(id+"F5.opExtrude","SWEPT_FACE",FACE,{"disambiguationData":[OSD([sQuery(id+"F4.wireOp",EDGE,"E40.MirrorCS")])]})]});
            var Q113;
            Q113=makeQuery(id+"F5.boolean.opBoolean","INTERSECT",EDGE,{"derivedFrom":[makeQuery(id+"F2.opExtrude","CAP_FACE",FACE,{"disambiguationData":[OSD([sQuery(id+"F0.wireOp",EDGE,"E5"),sQuery(id+"F0.wireOp",EDGE,"E6"),sQuery(id+"F0.wireOp",EDGE,"E7.filletArc"),sQuery(id+"F0.wireOp",EDGE,"E8.MirrorCS"),sQuery(id+"F0.wireOp",EDGE,"E12.MirrorCS"),sQuery(id+"F0.wireOp",EDGE,"E14.MirrorCS"),sQuery(id+"F0.wireOp",EDGE,"E16.MirrorCS"),sQuery(id+"F0.wireOp",EDGE,"E17.MirrorCS"),sQuery(id+"F0.wireOp",EDGE,"E19.MirrorCS"),sQuery(id+"F0.wireOp",EDGE,"E26.MirrorCS"),sQuery(id+"F0.wireOp",EDGE,"E27.MirrorCS"),sQuery(id+"F0.wireOp",EDGE,"E29.MirrorCS")])],"isStart":true}),makeQuery(id+"F5.opExtrude","SWEPT_FACE",FACE,{"disambiguationData":[OSD([sQuery(id+"F4.wireOp",EDGE,"E41.MirrorCS")])]})]});
            var Q114;
            Q114=makeQuery(id+"F5.boolean.opBoolean","INTERSECT",EDGE,{"derivedFrom":[makeQuery(id+"F2.opExtrude","CAP_FACE",FACE,{"disambiguationData":[OSD([sQuery(id+"F0.wireOp",EDGE,"E5"),sQuery(id+"F0.wireOp",EDGE,"E6"),sQuery(id+"F0.wireOp",EDGE,"E7.filletArc"),sQuery(id+"F0.wireOp",EDGE,"E8.MirrorCS"),sQuery(id+"F0.wireOp",EDGE,"E12.MirrorCS"),sQuery(id+"F0.wireOp",EDGE,"E14.MirrorCS"),sQuery(id+"F0.wireOp",EDGE,"E16.MirrorCS"),sQuery(id+"F0.wireOp",EDGE,"E17.MirrorCS"),sQuery(id+"F0.wireOp",EDGE,"E19.MirrorCS"),sQuery(id+"F0.wireOp",EDGE,"E26.MirrorCS"),sQuery(id+"F0.wireOp",EDGE,"E27.MirrorCS"),sQuery(id+"F0.wireOp",EDGE,"E29.MirrorCS")])],"isStart":true}),makeQuery(id+"F5.opExtrude","SWEPT_FACE",FACE,{"disambiguationData":[OSD([sQuery(id+"F4.wireOp",EDGE,"E42.MirrorCS")])]})]});
            var Q115;
            Q115=makeQuery(id+"F5.boolean.opBoolean","INTERSECT",EDGE,{"derivedFrom":[makeQuery(id+"F2.opExtrude","CAP_FACE",FACE,{"disambiguationData":[OSD([sQuery(id+"F0.wireOp",EDGE,"E5"),sQuery(id+"F0.wireOp",EDGE,"E6"),sQuery(id+"F0.wireOp",EDGE,"E7.filletArc"),sQuery(id+"F0.wireOp",EDGE,"E8.MirrorCS"),sQuery(id+"F0.wireOp",EDGE,"E12.MirrorCS"),sQuery(id+"F0.wireOp",EDGE,"E14.MirrorCS"),sQuery(id+"F0.wireOp",EDGE,"E16.MirrorCS"),sQuery(id+"F0.wireOp",EDGE,"E17.MirrorCS"),sQuery(id+"F0.wireOp",EDGE,"E19.MirrorCS"),sQuery(id+"F0.wireOp",EDGE,"E26.MirrorCS"),sQuery(id+"F0.wireOp",EDGE,"E27.MirrorCS"),sQuery(id+"F0.wireOp",EDGE,"E29.MirrorCS")])],"isStart":true}),makeQuery(id+"F5.opExtrude","SWEPT_FACE",FACE,{"disambiguationData":[OSD([sQuery(id+"F4.wireOp",EDGE,"E75.MirrorCS")])]})]});
            var Q116;
            Q116=makeQuery(id+"F5.boolean.opBoolean","INTERSECT",EDGE,{"derivedFrom":[makeQuery(id+"F2.opExtrude","CAP_FACE",FACE,{"disambiguationData":[OSD([sQuery(id+"F0.wireOp",EDGE,"E5"),sQuery(id+"F0.wireOp",EDGE,"E6"),sQuery(id+"F0.wireOp",EDGE,"E7.filletArc"),sQuery(id+"F0.wireOp",EDGE,"E8.MirrorCS"),sQuery(id+"F0.wireOp",EDGE,"E12.MirrorCS"),sQuery(id+"F0.wireOp",EDGE,"E14.MirrorCS"),sQuery(id+"F0.wireOp",EDGE,"E16.MirrorCS"),sQuery(id+"F0.wireOp",EDGE,"E17.MirrorCS"),sQuery(id+"F0.wireOp",EDGE,"E19.MirrorCS"),sQuery(id+"F0.wireOp",EDGE,"E26.MirrorCS"),sQuery(id+"F0.wireOp",EDGE,"E27.MirrorCS"),sQuery(id+"F0.wireOp",EDGE,"E29.MirrorCS")])],"isStart":true}),makeQuery(id+"F5.opExtrude","SWEPT_FACE",FACE,{"disambiguationData":[OSD([sQuery(id+"F4.wireOp",EDGE,"E70.MirrorCS")])]})]});
            var Q117;
            Q117=makeQuery(id+"F5.boolean.opBoolean","INTERSECT",EDGE,{"derivedFrom":[makeQuery(id+"F2.opExtrude","CAP_FACE",FACE,{"disambiguationData":[OSD([sQuery(id+"F0.wireOp",EDGE,"E5"),sQuery(id+"F0.wireOp",EDGE,"E6"),sQuery(id+"F0.wireOp",EDGE,"E7.filletArc"),sQuery(id+"F0.wireOp",EDGE,"E8.MirrorCS"),sQuery(id+"F0.wireOp",EDGE,"E12.MirrorCS"),sQuery(id+"F0.wireOp",EDGE,"E14.MirrorCS"),sQuery(id+"F0.wireOp",EDGE,"E16.MirrorCS"),sQuery(id+"F0.wireOp",EDGE,"E17.MirrorCS"),sQuery(id+"F0.wireOp",EDGE,"E19.MirrorCS"),sQuery(id+"F0.wireOp",EDGE,"E26.MirrorCS"),sQuery(id+"F0.wireOp",EDGE,"E27.MirrorCS"),sQuery(id+"F0.wireOp",EDGE,"E29.MirrorCS")])],"isStart":true}),makeQuery(id+"F5.opExtrude","SWEPT_FACE",FACE,{"disambiguationData":[OSD([sQuery(id+"F4.wireOp",EDGE,"E71.MirrorCS")])]})]});
            var Q118;
            Q118=makeQuery(id+"F5.boolean.opBoolean","INTERSECT",EDGE,{"derivedFrom":[makeQuery(id+"F2.opExtrude","CAP_FACE",FACE,{"disambiguationData":[OSD([sQuery(id+"F0.wireOp",EDGE,"E5"),sQuery(id+"F0.wireOp",EDGE,"E6"),sQuery(id+"F0.wireOp",EDGE,"E7.filletArc"),sQuery(id+"F0.wireOp",EDGE,"E8.MirrorCS"),sQuery(id+"F0.wireOp",EDGE,"E12.MirrorCS"),sQuery(id+"F0.wireOp",EDGE,"E14.MirrorCS"),sQuery(id+"F0.wireOp",EDGE,"E16.MirrorCS"),sQuery(id+"F0.wireOp",EDGE,"E17.MirrorCS"),sQuery(id+"F0.wireOp",EDGE,"E19.MirrorCS"),sQuery(id+"F0.wireOp",EDGE,"E26.MirrorCS"),sQuery(id+"F0.wireOp",EDGE,"E27.MirrorCS"),sQuery(id+"F0.wireOp",EDGE,"E29.MirrorCS")])],"isStart":true}),makeQuery(id+"F5.opExtrude","SWEPT_FACE",FACE,{"disambiguationData":[OSD([sQuery(id+"F4.wireOp",EDGE,"E72.MirrorCS")])]})]});
            var Q119;
            Q119=makeQuery(id+"F5.boolean.opBoolean","INTERSECT",EDGE,{"derivedFrom":[makeQuery(id+"F2.opExtrude","CAP_FACE",FACE,{"disambiguationData":[OSD([sQuery(id+"F0.wireOp",EDGE,"E5"),sQuery(id+"F0.wireOp",EDGE,"E6"),sQuery(id+"F0.wireOp",EDGE,"E7.filletArc"),sQuery(id+"F0.wireOp",EDGE,"E8.MirrorCS"),sQuery(id+"F0.wireOp",EDGE,"E12.MirrorCS"),sQuery(id+"F0.wireOp",EDGE,"E14.MirrorCS"),sQuery(id+"F0.wireOp",EDGE,"E16.MirrorCS"),sQuery(id+"F0.wireOp",EDGE,"E17.MirrorCS"),sQuery(id+"F0.wireOp",EDGE,"E19.MirrorCS"),sQuery(id+"F0.wireOp",EDGE,"E26.MirrorCS"),sQuery(id+"F0.wireOp",EDGE,"E27.MirrorCS"),sQuery(id+"F0.wireOp",EDGE,"E29.MirrorCS")])],"isStart":true}),makeQuery(id+"F5.opExtrude","SWEPT_FACE",FACE,{"disambiguationData":[OSD([sQuery(id+"F4.wireOp",EDGE,"E73.MirrorCS")])]})]});
            var Q120;
            Q120=makeQuery(id+"F5.boolean.opBoolean","INTERSECT",EDGE,{"derivedFrom":[makeQuery(id+"F2.opExtrude","CAP_FACE",FACE,{"disambiguationData":[OSD([sQuery(id+"F0.wireOp",EDGE,"E5"),sQuery(id+"F0.wireOp",EDGE,"E6"),sQuery(id+"F0.wireOp",EDGE,"E7.filletArc"),sQuery(id+"F0.wireOp",EDGE,"E8.MirrorCS"),sQuery(id+"F0.wireOp",EDGE,"E12.MirrorCS"),sQuery(id+"F0.wireOp",EDGE,"E14.MirrorCS"),sQuery(id+"F0.wireOp",EDGE,"E16.MirrorCS"),sQuery(id+"F0.wireOp",EDGE,"E17.MirrorCS"),sQuery(id+"F0.wireOp",EDGE,"E19.MirrorCS"),sQuery(id+"F0.wireOp",EDGE,"E26.MirrorCS"),sQuery(id+"F0.wireOp",EDGE,"E27.MirrorCS"),sQuery(id+"F0.wireOp",EDGE,"E29.MirrorCS")])],"isStart":true}),makeQuery(id+"F5.opExtrude","SWEPT_FACE",FACE,{"disambiguationData":[OSD([sQuery(id+"F4.wireOp",EDGE,"E74.MirrorCS")])]})]});
            var Q121;
            Q121=makeQuery(id+"F5.boolean.opBoolean","INTERSECT",EDGE,{"derivedFrom":[makeQuery(id+"F2.opExtrude","CAP_FACE",FACE,{"disambiguationData":[OSD([sQuery(id+"F0.wireOp",EDGE,"E5"),sQuery(id+"F0.wireOp",EDGE,"E6"),sQuery(id+"F0.wireOp",EDGE,"E7.filletArc"),sQuery(id+"F0.wireOp",EDGE,"E8.MirrorCS"),sQuery(id+"F0.wireOp",EDGE,"E12.MirrorCS"),sQuery(id+"F0.wireOp",EDGE,"E14.MirrorCS"),sQuery(id+"F0.wireOp",EDGE,"E16.MirrorCS"),sQuery(id+"F0.wireOp",EDGE,"E17.MirrorCS"),sQuery(id+"F0.wireOp",EDGE,"E19.MirrorCS"),sQuery(id+"F0.wireOp",EDGE,"E26.MirrorCS"),sQuery(id+"F0.wireOp",EDGE,"E27.MirrorCS"),sQuery(id+"F0.wireOp",EDGE,"E29.MirrorCS")])],"isStart":true}),makeQuery(id+"F5.opExtrude","SWEPT_FACE",FACE,{"disambiguationData":[OSD([sQuery(id+"F4.wireOp",EDGE,"E45.MirrorCS")])]})]});
            fillet(context, id + "F6", {"entities" : qUnion([Q0, Q1, Q2, Q3, Q4, Q5, Q6, Q7, Q8, Q9, Q10, Q11, Q12, Q13, Q14, Q15, Q16, Q17, Q18, Q19, Q20, Q21, Q22, Q23, Q24, Q25, Q26, Q27, Q28, Q29, Q30, Q31, Q32, Q33, Q34, Q35, Q36, Q37, Q38, Q39, Q40, Q41, Q42, Q43, Q44, Q45, Q46, Q47, Q48, Q49, Q50, Q51, Q52, Q53, Q54, Q55, Q56, Q57, Q58, Q59, Q60, Q61, Q62, Q63, Q64, Q65, Q66, Q67, Q68, Q69, Q70, Q71, Q72, Q73, Q74, Q75, Q76, Q77, Q78, Q79, Q80, Q81, Q82, Q83, Q84, Q85, Q86, Q87, Q88, Q89, Q90, Q91, Q92, Q93, Q94, Q95, Q96, Q97, Q98, Q99, Q100, Q101, Q102, Q103, Q104, Q105, Q106, Q107, Q108, Q109, Q110, Q111, Q112, Q113, Q114, Q115, Q116, Q117, Q118, Q119, Q120, Q121]), "radius" : 1 * mm, "tangentPropagation" : true, "allowEdgeOverflow" : false});
        }
        {
            var Q0;
            Q0=makeQuery(id+"F1.opExtrude","CAP_EDGE",EDGE,{"disambiguationData":[OSD([sQuery(id+"F0.wireOp",EDGE,"E34")])],"isStart":false});
            var Q1;
            Q1=makeQuery(id+"F1.opExtrude","CAP_EDGE",EDGE,{"disambiguationData":[OSD([sQuery(id+"F0.wireOp",EDGE,"E23.MirrorCS")])],"isStart":false});
            var Q2;
            Q2=makeQuery(id+"F1.opExtrude","CAP_EDGE",EDGE,{"disambiguationData":[OSD([sQuery(id+"F0.wireOp",EDGE,"E21.MirrorCS")])],"isStart":false});
            var Q3;
            Q3=makeQuery(id+"F1.opExtrude","CAP_FACE",FACE,{"disambiguationData":[OSD([sQuery(id+"F0.wireOp",EDGE,"E1"),sQuery(id+"F0.wireOp",EDGE,"E2"),sQuery(id+"F0.wireOp",EDGE,"E9.MirrorC"),sQuery(id+"F0.wireOp",EDGE,"E13.MirrorCS"),sQuery(id+"F0.wireOp",EDGE,"E35.MirrorCS")])],"isStart":false});
            fillet(context, id + "F7", {"entities" : qUnion([Q0, Q1, Q2, Q3]), "radius" : 0.1 * mm, "tangentPropagation" : true, "allowEdgeOverflow" : false});
        }
    });
